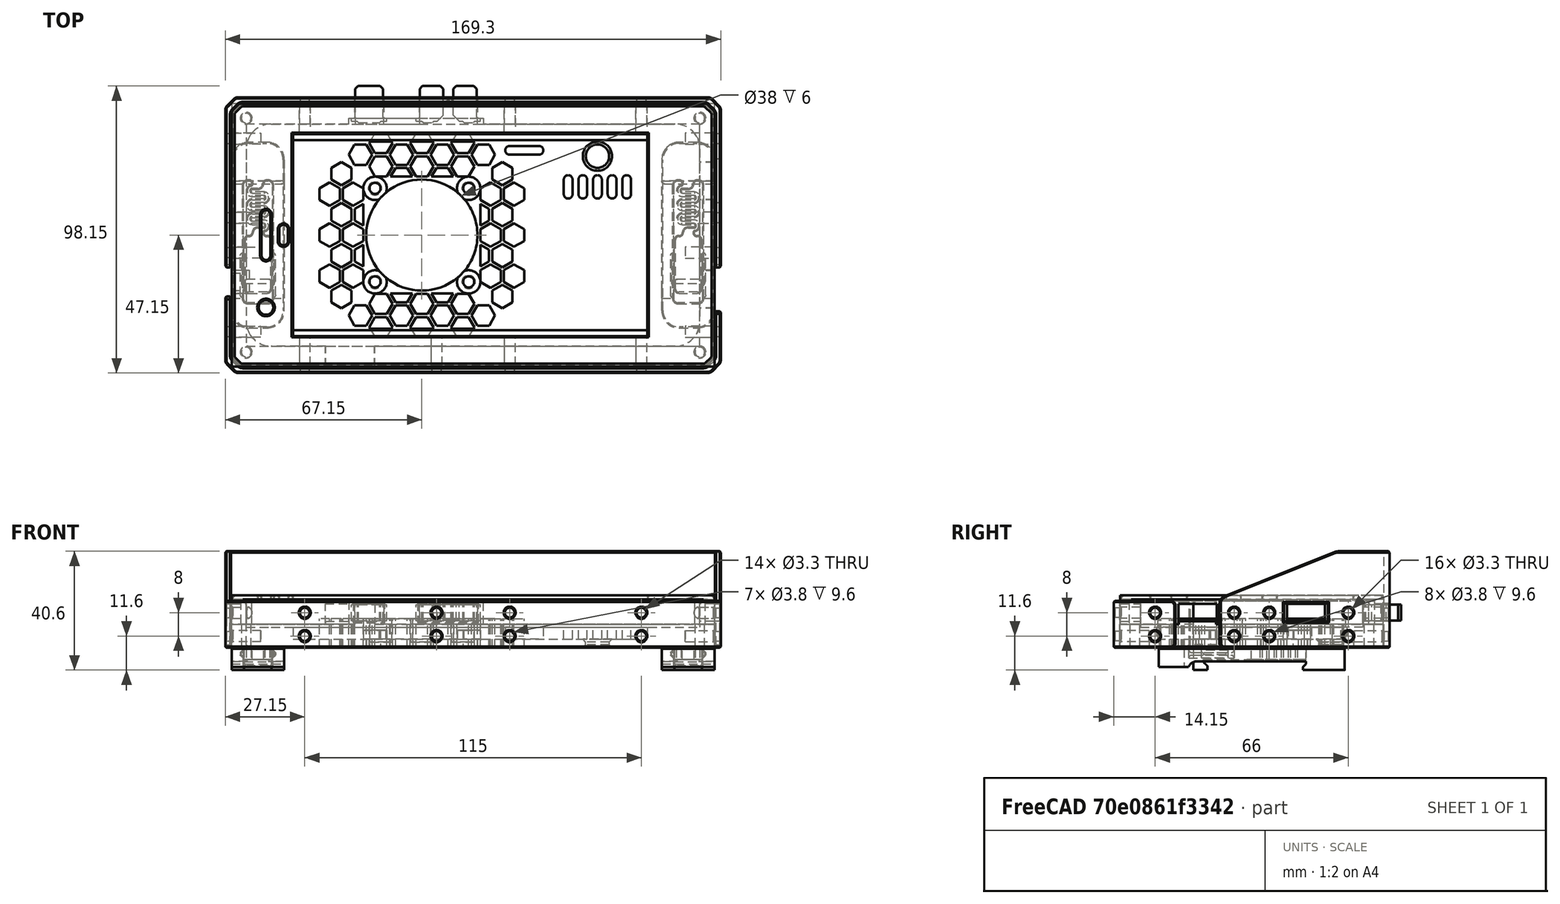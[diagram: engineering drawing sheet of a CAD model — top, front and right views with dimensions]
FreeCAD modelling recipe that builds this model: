
FCSTD DOCUMENT  (FreeCAD 0.19R24291 (Git))
Label: pixel-xl-navi-case
License: Other
LicenseURL: GPL3
objects: Sketcher::SketchObject×37, PartDesign::Pocket×27, PartDesign::Chamfer×20, Part::Box×14, PartDesign::Plane×12, PartDesign::Pad×10, PartDesign::Fillet×9, Part::Feature×8, Part::Chamfer×5, Part::MultiFuse×4, PartDesign::Body×4, Part::Cut×2, Spreadsheet::Sheet×1, Mesh::Feature×1, Part::FeaturePython×1
note: 219 computed .brp shape members not serialized (recipe doc carries the construction recipe); baked Part::Feature solids carry a one-line shape summary decoded from their .brp

FEATURE [Spreadsheet::Sheet] Spreadsheet  label="args"
  cells = A2=pixel width; B2(pixel_w)=155; A3=pixel heigh; B3(pixel_h)=76; A4=pixel thickness; B4(pixel_t)=8; A5=top screen offset; B5(screen_top_offset)=16; A6=bottom screen offset; B6(screen_bottom_offset)=17; A7=side screen offset; B7(screen_side_offset)=3.5; A8=power button offset; B8(button_power_offset)=37; A9=volume button offset; B9(button_volume_offset)=59; A10=power button width; B10(button_power_width)=10; A11=volume button width; B11(button_volume_width)=20; A12=screen width; B12(screen_width)=121; A13=screen heigh; B13(screen_heigh)=69; A14=pixel corner radius; B14(pixel_corner_radius)=8.5; A18=case thickness; B18(case_thickness)=10; A19=case width offset; B19(case_width_offset)=5; A20=case heigh offset; B20(case_heigh_offset)=7; A21=case corner radius; B21(case_corner_radius)=3; A23=front speaker offset; B23(front_speaker_offset)=5.75; A24=front speaker width; B24(front_speaker_width)=2; A25=front speaker heigh; B25(front_speaker_heigh)=16; A27=light sensor width; B27(light_sensor_width)=2; A28=light sensor heigh; B28(light_sensor_heigh)=6; A29=light sensor offset; B29(light_sensor_offset)=11.75; A31=camera x offset; B31(camera_x_offset)=6.75; A32=camera y offset; B32(camera_y_offset)=13.25; A33=camera radius; B33(camera_radius)=2; A35=speaker offset; B35(spekaer_offset)=14; A36=speaker width; B36(speaker_width)=11; A39=back thickness; B39(back_thickness)=8; A41=fan offset; B41(fan_offset)=60; A43=wiring hole offset; B43(wiring_hole_offset)=120; A44=wiring hole radius; B44(wiring_hole_radius)=4; A46=sim slot offset; B46(sim_slot_offset)=28; A47=sim slot width; B47(sim_slot_width)=15; A49=headphone jack center offset; B49(headphone_jack_center_offset)=22; A50=headphone jack radius; B50(headphone_jack_radius)=5; A51=headphone_jack_width; B51(headphone_jack_width)=8; A53=sun visor heigh; B53(sun_visor_heigh)=15; A54=sun visor ramp width; B54(sun_visor_ramp_width)=40
FEATURE [Sketcher::SketchObject] Sketch
  FullyConstrained = true
  MapMode = 5
  Support = -> [XY_Plane]
  expr: Constraints[11] = <<args>>.pixel_w + <<args>>.case_width_offset
  expr: Constraints[10] = <<args>>.pixel_h + <<args>>.case_heigh_offset
  expr: Constraints[9] = <<args>>.case_width_offset
  expr: Constraints[8] = <<args>>.case_heigh_offset
  sketch-geometry (4):
    g0: LineSegment StartX=-5 StartY=-7 StartZ=0 EndX=160 EndY=-7 EndZ=0
    g1: LineSegment StartX=160 StartY=-7 StartZ=0 EndX=160 EndY=83 EndZ=0
    g2: LineSegment StartX=160 StartY=83 StartZ=0 EndX=-5 EndY=83 EndZ=0
    g3: LineSegment StartX=-5 StartY=83 StartZ=0 EndX=-5 EndY=-7 EndZ=0
  constraints (12):
    c: Coincident(g0,g1)
    c: Coincident(g1,g2)
    c: Coincident(g2,g3)
    c: Coincident(g3,g0)
    c: Horizontal(g0)
    c: Horizontal(g2)
    c: Vertical(g1)
    c: Vertical(g3)
    c: DistanceY(g0,g-1) = 7
    c: DistanceX(g0,g-1) = 5
    c: DistanceY(g-1,g2) = 83
    c: DistanceX(g-1,g1) = 160
FEATURE [PartDesign::Pad] Pad
  Direction = (1,1,1)
  Length = 10
  Length2 = 100
  Profile = -> Sketch
  Type = 0
  expr: Length = <<args>>.case_thickness
FEATURE [PartDesign::Plane] DatumPlane  label="face-plane"
  AttachmentOffset = pos=(0,0,10) rot=(0,0,1;0rad)
  Length = 213.27
  MapMode = 5
  Placement = pos=(0,0,10) rot=(0,0,1;0rad)
  ResizeMode = 0
  Support = -> [XY_Plane]
  Width = 136.27
  expr: .AttachmentOffset.Base.z = <<args>>.case_thickness
FEATURE [Sketcher::SketchObject] Sketch001
  FullyConstrained = true
  MapMode = 5
  Placement = pos=(0,0,10) rot=(0,0,1;0rad)
  Support = -> [DatumPlane]
  expr: Constraints[11] = <<args>>.screen_heigh
  expr: Constraints[10] = <<args>>.screen_width
  expr: Constraints[9] = <<args>>.screen_side_offset
  expr: Constraints[8] = <<args>>.screen_top_offset
  sketch-geometry (4):
    g0: LineSegment StartX=16 StartY=72.5 StartZ=0 EndX=137 EndY=72.5 EndZ=0
    g1: LineSegment StartX=137 StartY=72.5 StartZ=0 EndX=137 EndY=3.5 EndZ=0
    g2: LineSegment StartX=137 StartY=3.5 StartZ=0 EndX=16 EndY=3.5 EndZ=0
    g3: LineSegment StartX=16 StartY=3.5 StartZ=0 EndX=16 EndY=72.5 EndZ=0
  constraints (12):
    c: Coincident(g0,g1)
    c: Coincident(g1,g2)
    c: Coincident(g2,g3)
    c: Coincident(g3,g0)
    c: Horizontal(g0)
    c: Horizontal(g2)
    c: Vertical(g1)
    c: Vertical(g3)
    c: DistanceX(g-1,g2) = 16
    c: DistanceY(g-1,g2) = 3.5
    c: DistanceX(g0,g0) = 121
    c: DistanceY(g1,g1) = 69
FEATURE [PartDesign::Pocket] Pocket
  BaseFeature = -> Pad
  Length = 5
  Length2 = 100
  Profile = -> Sketch001
  Type = 1
FEATURE [PartDesign::Plane] DatumPlane001  label="zero-plane"
  Length = 213.27
  MapMode = 5
  ResizeMode = 0
  Support = -> [XY_Plane]
  Width = 136.27
FEATURE [Sketcher::SketchObject] Sketch002
  FullyConstrained = true
  MapMode = 5
  Support = -> [DatumPlane001]
  expr: Constraints[10] = <<args>>.pixel_h
  expr: Constraints[9] = <<args>>.pixel_w
  sketch-geometry (4):
    g0: LineSegment StartX=0 StartY=0 StartZ=0 EndX=155 EndY=0 EndZ=0
    g1: LineSegment StartX=155 StartY=0 StartZ=0 EndX=155 EndY=76 EndZ=0
    g2: LineSegment StartX=155 StartY=76 StartZ=0 EndX=0 EndY=76 EndZ=0
    g3: LineSegment StartX=0 StartY=76 StartZ=0 EndX=0 EndY=0 EndZ=0
  constraints (11):
    c: Coincident(g0,g1)
    c: Coincident(g1,g2)
    c: Coincident(g2,g3)
    c: Coincident(g3,g0)
    c: Horizontal(g0)
    c: Horizontal(g2)
    c: Vertical(g1)
    c: Vertical(g3)
    c: Coincident(g0,g-1)
    c: DistanceX(g2,g2) = 155
    c: DistanceY(g1,g1) = 76
FEATURE [PartDesign::Pocket] Pocket001
  BaseFeature = -> Pocket
  Length = 8
  Length2 = 100
  Profile = -> Sketch002
  Reversed = true
  Type = 0
  expr: Length = <<args>>.case_thickness - 2
FEATURE [Sketcher::SketchObject] Sketch003
  FullyConstrained = true
  MapMode = 5
  Placement = pos=(0,0,10) rot=(0,0,1;0rad)
  Support = -> [DatumPlane]
  expr: Constraints[21] = <<args>>.light_sensor_heigh - <<args>>.light_sensor_width
  expr: Constraints[19] = <<args>>.light_sensor_width / 2 + 0.5
  expr: Constraints[18] = <<args>>.front_speaker_width / 2 + 0.5
  expr: Constraints[16] = (<<args>>.pixel_h - <<args>>.front_speaker_heigh) / 2 + <<args>>.front_speaker_width / 2
  expr: Constraints[20] = <<args>>.light_sensor_offset + <<args>>.light_sensor_width / 2
  expr: Constraints[15] = <<args>>.front_speaker_offset + <<args>>.front_speaker_width / 2
  expr: Constraints[22] = (<<args>>.pixel_h - <<args>>.light_sensor_heigh) / 2 + <<args>>.light_sensor_width / 2
  expr: Constraints[17] = <<args>>.front_speaker_heigh - <<args>>.front_speaker_width
  expr: Constraints[14] = <<args>>.camera_y_offset
  expr: Constraints[13] = <<args>>.camera_x_offset
  expr: Constraints[12] = <<args>>.camera_radius + 0.5
  sketch-geometry (9):
    g0: ArcOfCircle CenterX=6.75 CenterY=45 CenterZ=0 NormalX=0 NormalY=0 NormalZ=1 AngleXU=0 Radius=1.5 StartAngle=2e-16 EndAngle=3.14159
    g1: ArcOfCircle CenterX=6.75 CenterY=31 CenterZ=0 NormalX=0 NormalY=0 NormalZ=1 AngleXU=0 Radius=1.5 StartAngle=3.14159 EndAngle=6.28319
    g2: LineSegment StartX=5.25 StartY=45 StartZ=0 EndX=5.25 EndY=31 EndZ=0
    g3: LineSegment StartX=8.25 StartY=45 StartZ=0 EndX=8.25 EndY=31 EndZ=0
    g4: ArcOfCircle CenterX=12.75 CenterY=40 CenterZ=0 NormalX=0 NormalY=0 NormalZ=1 AngleXU=0 Radius=1.5 StartAngle=2.4e-15 EndAngle=3.14159
    g5: ArcOfCircle CenterX=12.75 CenterY=36 CenterZ=0 NormalX=0 NormalY=0 NormalZ=1 AngleXU=0 Radius=1.5 StartAngle=3.14159 EndAngle=6.28319
    g6: LineSegment StartX=11.25 StartY=40 StartZ=0 EndX=11.25 EndY=36 EndZ=0
    g7: LineSegment StartX=14.25 StartY=40 StartZ=0 EndX=14.25 EndY=36 EndZ=0
    g8: Circle CenterX=6.75 CenterY=13.25 CenterZ=0 NormalX=0 NormalY=0 NormalZ=1 AngleXU=0 Radius=2.5
  constraints (23):
    c: Tangent(g0,g3) = 1.5708
    c: Tangent(g0,g2) = -1.5708
    c: Tangent(g2,g1) = -1.5708
    c: Tangent(g3,g1) = 1.5708
    c: Vertical(g2)
    c: Equal(g0,g1)
    c: Tangent(g4,g7) = 1.5708
    c: Tangent(g4,g6) = -1.5708
    c: Tangent(g6,g5) = -1.5708
    c: Tangent(g7,g5) = 1.5708
    c: Vertical(g6)
    c: Equal(g4,g5)
    c: Radius(g8) = 2.5
    c: DistanceX(g-1,g8) = 6.75
    c: DistanceY(g-1,g8) = 13.25
    c: DistanceX(g-1,g1) = 6.75
    c: DistanceY(g-1,g1) = 31
    c: DistanceY(g1,g0) = 14
    c: Radius(g0) = 1.5
    c: Radius(g4) = 1.5
    c: DistanceX(g-1,g5) = 12.75
    c: DistanceY(g5,g4) = 4
    c: DistanceY(g-1,g5) = 36
FEATURE [PartDesign::Pocket] Pocket002
  BaseFeature = -> Pocket001
  Length = 5
  Length2 = 100
  Profile = -> Sketch003
  Type = 1
FEATURE [PartDesign::Plane] DatumPlane002  label="right-edge-plane"
  AttachmentOffset = pos=(0,0,-83) rot=(0,0,1;0rad)
  Length = 204.235
  MapMode = 5
  Placement = pos=(0,83,1.84e-14) rot=(1,0,0;1.5708rad)
  ResizeMode = 0
  Support = -> [XZ_Plane]
  Width = 69.2354
  expr: .AttachmentOffset.Base.z = -(<<args>>.pixel_h + <<args>>.case_heigh_offset)
FEATURE [Sketcher::SketchObject] Sketch007
  FullyConstrained = true
  MapMode = 5
  Placement = pos=(0,83,1.84e-14) rot=(1,0,0;1.5708rad)
  Support = -> [DatumPlane002]
  expr: Constraints[16] = <<args>>.button_power_width
  expr: Constraints[17] = <<args>>.button_volume_width
  expr: Constraints[18] = <<args>>.button_volume_offset
  expr: Constraints[19] = <<args>>.button_power_offset
  sketch-geometry (8):
    g0: LineSegment StartX=37 StartY=7 StartZ=0 EndX=47 EndY=7 EndZ=0
    g1: LineSegment StartX=47 StartY=7 StartZ=0 EndX=47 EndY=0 EndZ=0
    g2: LineSegment StartX=47 StartY=0 StartZ=0 EndX=37 EndY=0 EndZ=0
    g3: LineSegment StartX=37 StartY=0 StartZ=0 EndX=37 EndY=7 EndZ=0
    g4: LineSegment StartX=59 StartY=7 StartZ=0 EndX=79 EndY=7 EndZ=0
    g5: LineSegment StartX=79 StartY=7 StartZ=0 EndX=79 EndY=0 EndZ=0
    g6: LineSegment StartX=79 StartY=0 StartZ=0 EndX=59 EndY=0 EndZ=0
    g7: LineSegment StartX=59 StartY=0 StartZ=0 EndX=59 EndY=7 EndZ=0
  constraints (24):
    c: Coincident(g0,g1)
    c: Coincident(g1,g2)
    c: Coincident(g2,g3)
    c: Coincident(g3,g0)
    c: Horizontal(g0)
    c: Horizontal(g2)
    c: Vertical(g1)
    c: Vertical(g3)
    c: Coincident(g4,g5)
    c: Coincident(g5,g6)
    c: Coincident(g6,g7)
    c: Coincident(g7,g4)
    c: Horizontal(g4)
    c: Horizontal(g6)
    c: Vertical(g5)
    c: Vertical(g7)
    c: DistanceX(g2,g2) = 10
    c: DistanceX(g6,g6) = 20
    c: DistanceX(g-1,g6) = 59
    c: DistanceX(g-1,g2) = 37
    c: DistanceY(g-1,g2) = 0
    c: DistanceY(g-1,g6) = 0
    c: DistanceY(g3,g3) = 7
    c: DistanceY(g7,g7) = 7
FEATURE [PartDesign::Plane] DatumPlane003  label="bottom-edge-plane"
  AttachmentOffset = pos=(0,0,160) rot=(0,0,1;0rad)
  Length = 122.697
  MapMode = 5
  Placement = pos=(160,-3.55e-14,3.55e-14) rot=(0.57735,0.57735,0.57735;2.0944rad)
  ResizeMode = 0
  Support = -> [YZ_Plane]
  Width = 64.6969
  expr: .AttachmentOffset.Base.z = <<args>>.pixel_w + <<args>>.case_width_offset
FEATURE [Sketcher::SketchObject] Sketch008
  FullyConstrained = true
  MapMode = 5
  Placement = pos=(160,-3.55e-14,3.55e-14) rot=(0.57735,0.57735,0.57735;2.0944rad)
  Support = -> [DatumPlane003]
  expr: Constraints[18] = <<args>>.speaker_width + 2
  expr: Constraints[19] = <<args>>.speaker_width + 2
  expr: Constraints[23] = <<args>>.pixel_h - (<<args>>.spekaer_offset + <<args>>.speaker_width + 2 - 1)
  expr: Constraints[20] = <<args>>.spekaer_offset - 1
  sketch-geometry (8):
    g0: LineSegment StartX=13 StartY=0 StartZ=0 EndX=26 EndY=0 EndZ=0
    g1: LineSegment StartX=26 StartY=0 StartZ=0 EndX=26 EndY=7 EndZ=0
    g2: LineSegment StartX=26 StartY=7 StartZ=0 EndX=13 EndY=7 EndZ=0
    g3: LineSegment StartX=13 StartY=7 StartZ=0 EndX=13 EndY=0 EndZ=0
    g4: LineSegment StartX=50 StartY=0 StartZ=0 EndX=63 EndY=0 EndZ=0
    g5: LineSegment StartX=63 StartY=0 StartZ=0 EndX=63 EndY=7 EndZ=0
    g6: LineSegment StartX=63 StartY=7 StartZ=0 EndX=50 EndY=7 EndZ=0
    g7: LineSegment StartX=50 StartY=7 StartZ=0 EndX=50 EndY=0 EndZ=0
  constraints (24):
    c: Coincident(g0,g1)
    c: Coincident(g1,g2)
    c: Coincident(g2,g3)
    c: Coincident(g3,g0)
    c: Horizontal(g0)
    c: Horizontal(g2)
    c: Vertical(g1)
    c: Vertical(g3)
    c: Coincident(g4,g5)
    c: Coincident(g5,g6)
    c: Coincident(g6,g7)
    c: Coincident(g7,g4)
    c: Horizontal(g4)
    c: Horizontal(g6)
    c: Vertical(g5)
    c: Vertical(g7)
    c: DistanceY(g-1,g0) = 0
    c: DistanceY(g-1,g4) = 0
    c: DistanceX(g2,g2) = 13
    c: DistanceX(g6,g6) = 13
    c: DistanceX(g-1,g0) = 13
    c: DistanceY(g1,g1) = 7
    c: DistanceY(g7,g7) = 7
    c: DistanceX(g-1,g4) = 50
FEATURE [Mesh::Feature] PixelXL
  Placement = pos=(77,38,8) rot=(0.707107,-0.707107,0;3.14159rad)
FEATURE [PartDesign::Plane] DatumPlane004  label="left-edge-plane"
  AttachmentOffset = pos=(0,0,7) rot=(0,0,1;0rad)
  Length = 204.235
  MapMode = 5
  Placement = pos=(0,-7,-1.6e-15) rot=(1,0,0;1.5708rad)
  ResizeMode = 0
  Support = -> [XZ_Plane]
  Width = 69.2354
  expr: .AttachmentOffset.Base.z = <<args>>.case_heigh_offset
FEATURE [Sketcher::SketchObject] Sketch009
  FullyConstrained = true
  MapMode = 5
  Placement = pos=(0,-7,-1.6e-15) rot=(1,0,0;1.5708rad)
  Support = -> [DatumPlane004]
  expr: Constraints[8] = <<args>>.sim_slot_offset - 1
  expr: Constraints[9] = <<args>>.sim_slot_width + 2
  expr: Constraints[10] = <<args>>.pixel_t - 1
  sketch-geometry (4):
    g0: LineSegment StartX=27 StartY=7 StartZ=0 EndX=44 EndY=7 EndZ=0
    g1: LineSegment StartX=44 StartY=7 StartZ=0 EndX=44 EndY=0 EndZ=0
    g2: LineSegment StartX=44 StartY=0 StartZ=0 EndX=27 EndY=0 EndZ=0
    g3: LineSegment StartX=27 StartY=0 StartZ=0 EndX=27 EndY=7 EndZ=0
  constraints (12):
    c: Coincident(g0,g1)
    c: Coincident(g1,g2)
    c: Coincident(g2,g3)
    c: Coincident(g3,g0)
    c: Horizontal(g0)
    c: Horizontal(g2)
    c: Vertical(g1)
    c: Vertical(g3)
    c: DistanceX(g-1,g2) = 27
    c: DistanceX(g0,g0) = 17
    c: DistanceY(g1,g1) = 7
    c: DistanceY(g-1,g2) = 0
FEATURE [PartDesign::Plane] DatumPlane005  label="top-edge-plane"
  AttachmentOffset = pos=(0,0,-7) rot=(0,0,1;0rad)
  Length = 122.697
  MapMode = 5
  Placement = pos=(-7,1.6e-15,-1.6e-15) rot=(0.57735,0.57735,0.57735;2.0944rad)
  ResizeMode = 0
  Support = -> [YZ_Plane]
  Width = 64.6969
  expr: .AttachmentOffset.Base.z = -<<args>>.case_heigh_offset
FEATURE [Sketcher::SketchObject] Sketch010
  FullyConstrained = true
  MapMode = 5
  Placement = pos=(-7,1.6e-15,-1.6e-15) rot=(0.57735,0.57735,0.57735;2.0944rad)
  Support = -> [DatumPlane005]
  expr: Constraints[8] = <<args>>.headphone_jack_center_offset - <<args>>.headphone_jack_width / 2
  expr: Constraints[9] = <<args>>.headphone_jack_width
  expr: Constraints[10] = <<args>>.pixel_t
  sketch-geometry (4):
    g0: LineSegment StartX=18 StartY=8 StartZ=0 EndX=26 EndY=8 EndZ=0
    g1: LineSegment StartX=26 StartY=8 StartZ=0 EndX=26 EndY=0 EndZ=0
    g2: LineSegment StartX=26 StartY=0 StartZ=0 EndX=18 EndY=0 EndZ=0
    g3: LineSegment StartX=18 StartY=0 StartZ=0 EndX=18 EndY=8 EndZ=0
  constraints (12):
    c: Coincident(g0,g1)
    c: Coincident(g1,g2)
    c: Coincident(g2,g3)
    c: Coincident(g3,g0)
    c: Horizontal(g0)
    c: Horizontal(g2)
    c: Vertical(g1)
    c: Vertical(g3)
    c: DistanceX(g-1,g2) = 18
    c: DistanceX(g2,g2) = 8
    c: DistanceY(g3,g3) = 8
    c: DistanceY(g-1,g2) = 0
FEATURE [PartDesign::Plane] DatumPlane006  label="zero-plane001"
  Length = 213.27
  MapMode = 5
  ResizeMode = 0
  Support = -> [XY_Plane001]
  Width = 136.27
FEATURE [Sketcher::SketchObject] Sketch011
  FullyConstrained = true
  MapMode = 5
  Support = -> [DatumPlane006]
  expr: Constraints[11] = <<args>>.case_heigh_offset
  expr: Constraints[10] = <<args>>.case_width_offset
  expr: Constraints[9] = <<args>>.case_heigh_offset * 2 + <<args>>.pixel_h
  expr: Constraints[8] = <<args>>.case_width_offset * 2 + <<args>>.pixel_w
  sketch-geometry (4):
    g0: LineSegment StartX=-5 StartY=-7 StartZ=0 EndX=160 EndY=-7 EndZ=0
    g1: LineSegment StartX=160 StartY=-7 StartZ=0 EndX=160 EndY=83 EndZ=0
    g2: LineSegment StartX=160 StartY=83 StartZ=0 EndX=-5 EndY=83 EndZ=0
    g3: LineSegment StartX=-5 StartY=83 StartZ=0 EndX=-5 EndY=-7 EndZ=0
  constraints (12):
    c: Coincident(g0,g1)
    c: Coincident(g1,g2)
    c: Coincident(g2,g3)
    c: Coincident(g3,g0)
    c: Horizontal(g0)
    c: Horizontal(g2)
    c: Vertical(g1)
    c: Vertical(g3)
    c: DistanceX(g2,g2) = 165
    c: DistanceY(g1,g1) = 90
    c: DistanceX(g0,g-1) = 5
    c: DistanceY(g0,g-1) = 7
FEATURE [PartDesign::Pad] Pad001
  Direction = (1,1,1)
  Length = 8
  Length2 = 100
  Profile = -> Sketch011
  Type = 0
  expr: Length = <<args>>.back_thickness
FEATURE [PartDesign::Plane] DatumPlane007  label="inner-face-plane"
  AttachmentOffset = pos=(0,0,8) rot=(0,0,1;0rad)
  Length = 213.27
  MapMode = 5
  Placement = pos=(0,0,8) rot=(0,0,1;0rad)
  ResizeMode = 0
  Support = -> [XY_Plane001]
  Width = 136.27
  expr: .AttachmentOffset.Base.z = <<args>>.back_thickness
FEATURE [Sketcher::SketchObject] Sketch012
  FullyConstrained = true
  MapMode = 5
  Placement = pos=(0,0,8) rot=(0,0,1;0rad)
  Support = -> [DatumPlane007]
  expr: Constraints[11] = <<args>>.screen_top_offset
  expr: Constraints[10] = <<args>>.screen_side_offset + 2
  expr: Constraints[9] = <<args>>.screen_width
  expr: Constraints[8] = <<args>>.screen_heigh - 4
  sketch-geometry (4):
    g0: LineSegment StartX=16 StartY=5.5 StartZ=0 EndX=137 EndY=5.5 EndZ=0
    g1: LineSegment StartX=137 StartY=5.5 StartZ=0 EndX=137 EndY=70.5 EndZ=0
    g2: LineSegment StartX=137 StartY=70.5 StartZ=0 EndX=16 EndY=70.5 EndZ=0
    g3: LineSegment StartX=16 StartY=70.5 StartZ=0 EndX=16 EndY=5.5 EndZ=0
  constraints (12):
    c: Coincident(g0,g1)
    c: Coincident(g1,g2)
    c: Coincident(g2,g3)
    c: Coincident(g3,g0)
    c: Horizontal(g0)
    c: Horizontal(g2)
    c: Vertical(g1)
    c: Vertical(g3)
    c: DistanceY(g1,g1) = 65
    c: DistanceX(g2,g2) = 121
    c: DistanceY(g-1,g0) = 5.5
    c: DistanceX(g-1,g0) = 16
FEATURE [PartDesign::Pocket] Pocket009
  BaseFeature = -> Pad001
  Length = 5
  Length2 = 100
  Profile = -> Sketch012
  Type = 0
FEATURE [PartDesign::Plane] DatumPlane009  label="left-edge-plane001"
  AttachmentOffset = pos=(0,0,7) rot=(0,0,1;0rad)
  Length = 204.235
  MapMode = 5
  Placement = pos=(0,-7,-1.6e-15) rot=(1,0,0;1.5708rad)
  ResizeMode = 0
  Support = -> [XZ_Plane001]
  Width = 69.2354
  expr: .AttachmentOffset.Base.z = <<args>>.case_heigh_offset
FEATURE [PartDesign::Plane] DatumPlane010  label="top-edge-plane001"
  AttachmentOffset = pos=(0,0,-5) rot=(0,0,1;0rad)
  Length = 122.697
  MapMode = 5
  Placement = pos=(-5,1.1e-15,-1.1e-15) rot=(0.57735,0.57735,0.57735;2.0944rad)
  ResizeMode = 0
  Support = -> [YZ_Plane001]
  Width = 64.6969
  expr: .AttachmentOffset.Base.z = -<<args>>.case_width_offset
FEATURE [PartDesign::Plane] DatumPlane011  label="bottom-edge-plane001"
  AttachmentOffset = pos=(0,0,160) rot=(0,0,1;0rad)
  Length = 122.697
  MapMode = 5
  Placement = pos=(160,-3.55e-14,3.55e-14) rot=(0.57735,0.57735,0.57735;2.0944rad)
  ResizeMode = 0
  Support = -> [YZ_Plane001]
  Width = 64.6969
  expr: .AttachmentOffset.Base.z = <<args>>.pixel_w + <<args>>.case_width_offset
FEATURE [PartDesign::Plane] DatumPlane012  label="right-edge-plane001"
  AttachmentOffset = pos=(0,0,-83) rot=(0,0,1;0rad)
  Length = 204.235
  MapMode = 5
  Placement = pos=(0,83,1.84e-14) rot=(1,0,0;1.5708rad)
  ResizeMode = 0
  Support = -> [XZ_Plane001]
  Width = 69.2354
  expr: .AttachmentOffset.Base.z = -(<<args>>.pixel_h + <<args>>.case_heigh_offset)
FEATURE [Sketcher::SketchObject] Sketch013
  FullyConstrained = true
  MapMode = 5
  Placement = pos=(0,83,1.84e-14) rot=(1,0,0;1.5708rad)
  Support = -> [DatumPlane012]
  expr: Constraints[23] = <<args>>.button_volume_offset + 0.15
  expr: Constraints[21] = <<args>>.button_volume_width - 0.3
  expr: Constraints[20] = <<args>>.button_power_width - 0.3
  expr: Constraints[22] = <<args>>.button_power_offset + 0.15
  expr: Constraints[17] = <<args>>.back_thickness
  expr: Constraints[16] = <<args>>.back_thickness
  sketch-geometry (8):
    g0: LineSegment StartX=37.15 StartY=9 StartZ=0 EndX=46.85 EndY=9 EndZ=0
    g1: LineSegment StartX=46.85 StartY=9 StartZ=0 EndX=46.85 EndY=8 EndZ=0
    g2: LineSegment StartX=46.85 StartY=8 StartZ=0 EndX=37.15 EndY=8 EndZ=0
    g3: LineSegment StartX=37.15 StartY=8 StartZ=0 EndX=37.15 EndY=9 EndZ=0
    g4: LineSegment StartX=59.15 StartY=9 StartZ=0 EndX=78.85 EndY=9 EndZ=0
    g5: LineSegment StartX=78.85 StartY=9 StartZ=0 EndX=78.85 EndY=8 EndZ=0
    g6: LineSegment StartX=78.85 StartY=8 StartZ=0 EndX=59.15 EndY=8 EndZ=0
    g7: LineSegment StartX=59.15 StartY=8 StartZ=0 EndX=59.15 EndY=9 EndZ=0
  constraints (24):
    c: Coincident(g0,g1)
    c: Coincident(g1,g2)
    c: Coincident(g2,g3)
    c: Coincident(g3,g0)
    c: Horizontal(g0)
    c: Horizontal(g2)
    c: Vertical(g1)
    c: Vertical(g3)
    c: Coincident(g4,g5)
    c: Coincident(g5,g6)
    c: Coincident(g6,g7)
    c: Coincident(g7,g4)
    c: Horizontal(g4)
    c: Horizontal(g6)
    c: Vertical(g5)
    c: Vertical(g7)
    c: DistanceY(g-1,g2) = 8
    c: DistanceY(g-1,g6) = 8
    c: DistanceY(g3,g3) = 1
    c: DistanceY(g7,g7) = 1
    c: DistanceX(g0,g0) = 9.7
    c: DistanceX(g4,g4) = 19.7
    c: DistanceX(g-1,g2) = 37.15
    c: DistanceX(g-1,g6) = 59.15
FEATURE [PartDesign::Pad] Pad002  label="right-pad"
  BaseFeature = -> Pocket009
  Direction = (1,1,1)
  Length = 7
  Length2 = 100
  Profile = -> Sketch013
  Type = 0
  expr: Length = <<args>>.case_heigh_offset
FEATURE [Sketcher::SketchObject] Sketch014
  FullyConstrained = true
  MapMode = 5
  Placement = pos=(160,-3.55e-14,3.55e-14) rot=(0.57735,0.57735,0.57735;2.0944rad)
  Support = -> [DatumPlane011]
  expr: Constraints[23] = <<args>>.pixel_h - (<<args>>.spekaer_offset + <<args>>.speaker_width + 2 - 1) + 0.15
  expr: Constraints[19] = <<args>>.back_thickness
  expr: Constraints[18] = <<args>>.back_thickness
  expr: Constraints[22] = <<args>>.spekaer_offset + 0.15 - 1
  expr: Constraints[17] = <<args>>.speaker_width - 0.3 + 2
  expr: Constraints[16] = <<args>>.speaker_width - 0.3 + 2
  sketch-geometry (8):
    g0: LineSegment StartX=13.15 StartY=9 StartZ=0 EndX=25.85 EndY=9 EndZ=0
    g1: LineSegment StartX=25.85 StartY=9 StartZ=0 EndX=25.85 EndY=8 EndZ=0
    g2: LineSegment StartX=25.85 StartY=8 StartZ=0 EndX=13.15 EndY=8 EndZ=0
    g3: LineSegment StartX=13.15 StartY=8 StartZ=0 EndX=13.15 EndY=9 EndZ=0
    g4: LineSegment StartX=50.15 StartY=9 StartZ=0 EndX=62.85 EndY=9 EndZ=0
    g5: LineSegment StartX=62.85 StartY=9 StartZ=0 EndX=62.85 EndY=8 EndZ=0
    g6: LineSegment StartX=62.85 StartY=8 StartZ=0 EndX=50.15 EndY=8 EndZ=0
    g7: LineSegment StartX=50.15 StartY=8 StartZ=0 EndX=50.15 EndY=9 EndZ=0
  constraints (24):
    c: Coincident(g0,g1)
    c: Coincident(g1,g2)
    c: Coincident(g2,g3)
    c: Coincident(g3,g0)
    c: Horizontal(g0)
    c: Horizontal(g2)
    c: Vertical(g1)
    c: Vertical(g3)
    c: Coincident(g4,g5)
    c: Coincident(g5,g6)
    c: Coincident(g6,g7)
    c: Coincident(g7,g4)
    c: Horizontal(g4)
    c: Horizontal(g6)
    c: Vertical(g5)
    c: Vertical(g7)
    c: DistanceX(g0,g0) = 12.7
    c: DistanceX(g4,g4) = 12.7
    c: DistanceY(g-1,g2) = 8
    c: DistanceY(g-1,g6) = 8
    c: DistanceY(g3,g3) = 1
    c: DistanceY(g7,g7) = 1
    c: DistanceX(g-1,g2) = 13.15
    c: DistanceX(g-1,g6) = 50.15
FEATURE [PartDesign::Pad] Pad003  label="bottom-pad"
  BaseFeature = -> Pad002
  Direction = (1,1,1)
  Length = 5
  Length2 = 100
  Profile = -> Sketch014
  Reversed = true
  Type = 0
  expr: Length = <<args>>.case_width_offset
FEATURE [Sketcher::SketchObject] Sketch015
  FullyConstrained = true
  MapMode = 5
  Support = -> [DatumPlane001]
  expr: Constraints[11] = <<args>>.pixel_w
  expr: Constraints[10] = <<args>>.pixel_w
  expr: Constraints[8] = <<args>>.pixel_h + 2
  expr: Constraints[7] = <<args>>.pixel_h + 2
  sketch-geometry (4):
    g0: Circle CenterX=0 CenterY=-2 CenterZ=0 NormalX=0 NormalY=0 NormalZ=1 AngleXU=0 Radius=1.9
    g1: Circle CenterX=0 CenterY=78 CenterZ=0 NormalX=0 NormalY=0 NormalZ=1 AngleXU=0 Radius=1.9
    g2: Circle CenterX=155 CenterY=78 CenterZ=0 NormalX=0 NormalY=0 NormalZ=1 AngleXU=0 Radius=1.9
    g3: Circle CenterX=155 CenterY=-2 CenterZ=0 NormalX=0 NormalY=0 NormalZ=1 AngleXU=0 Radius=1.9
  constraints (12):
    c: Radius(g2) = 1.9
    c: Radius(g3) = 1.9
    c: Radius(g1) = 1.9
    c: Radius(g0) = 1.9
    c: DistanceY(g0,g-1) = 2
    c: DistanceX(g0,g-1) = 0
    c: DistanceX(g1,g-1) = 0
    c: DistanceY(g-1,g1) = 78
    c: DistanceY(g-1,g2) = 78
    c: DistanceY(g3,g0) = 0
    c: DistanceX(g-1,g2) = 155
    c: DistanceX(g-1,g3) = 155
FEATURE [Sketcher::SketchObject] Sketch016
  FullyConstrained = true
  MapMode = 5
  Support = -> [DatumPlane006]
  expr: Constraints[11] = <<args>>.pixel_w
  expr: Constraints[10] = <<args>>.pixel_w
  expr: Constraints[7] = <<args>>.pixel_h + 2
  expr: Constraints[6] = <<args>>.pixel_h + 2
  sketch-geometry (4):
    g0: Circle CenterX=0 CenterY=78 CenterZ=0 NormalX=0 NormalY=0 NormalZ=1 AngleXU=0 Radius=1.65
    g1: Circle CenterX=155 CenterY=78 CenterZ=0 NormalX=0 NormalY=0 NormalZ=1 AngleXU=0 Radius=1.65
    g2: Circle CenterX=155 CenterY=-2 CenterZ=0 NormalX=0 NormalY=0 NormalZ=1 AngleXU=0 Radius=1.65
    g3: Circle CenterX=0 CenterY=-2 CenterZ=0 NormalX=0 NormalY=0 NormalZ=1 AngleXU=0 Radius=1.65
  constraints (12):
    c: Radius(g3) = 1.65
    c: Radius(g0) = 1.65
    c: Radius(g1) = 1.65
    c: Radius(g2) = 1.65
    c: DistanceY(g3,g-1) = 2
    c: DistanceY(g2,g-1) = 2
    c: DistanceY(g-1,g0) = 78
    c: DistanceY(g-1,g1) = 78
    c: DistanceX(g0,g-1) = 0
    c: DistanceX(g-1,g3) = 0
    c: DistanceX(g-1,g2) = 155
    c: DistanceX(g0,g1) = 155
FEATURE [PartDesign::Pocket] Pocket011
  BaseFeature = -> Pad003
  Length = 5
  Length2 = 100
  Profile = -> Sketch016
  Reversed = true
  Type = 1
FEATURE [Part::Feature] Cut001001  label="hex-cut"
  Placement = pos=(70,58,0) rot=(0,0,1;0rad)
  shape: bbox 50 x 14.96 x 10 mm, 92 faces, 12 solids (baked)
FEATURE [Part::Feature] Cut001002  label="hex-cut001"
  Placement = pos=(70,18,0) rot=(0,0,1;3.14159rad)
  shape: bbox 50 x 14.96 x 10 mm, 92 faces, 12 solids (baked)
FEATURE [Part::Feature] Cut001003  label="hex-cut002"
  Placement = pos=(50,38,0) rot=(0,0,1;1.5708rad)
  shape: bbox 14.96 x 50 x 10 mm, 92 faces, 12 solids (baked)
FEATURE [Part::Feature] Cut001004  label="hex-cut003"
  Placement = pos=(90,38,0) rot=(0,0,-1;1.5708rad)
  shape: bbox 14.96 x 50 x 10 mm, 92 faces, 12 solids (baked)
FEATURE [Sketcher::SketchObject] Sketch017
  FullyConstrained = true
  MapMode = 5
  Support = -> [DatumPlane006]
  expr: Constraints[2] = <<args>>.fan_offset
  expr: Constraints[0] = <<args>>.pixel_h / 2
  sketch-geometry (5):
    g0: Circle CenterX=60 CenterY=38 CenterZ=0 NormalX=0 NormalY=0 NormalZ=1 AngleXU=0 Radius=19
    g1: Circle CenterX=44 CenterY=54 CenterZ=0 NormalX=0 NormalY=0 NormalZ=1 AngleXU=0 Radius=1.9
    g2: Circle CenterX=76 CenterY=54 CenterZ=0 NormalX=0 NormalY=0 NormalZ=1 AngleXU=0 Radius=1.9
    g3: Circle CenterX=76 CenterY=22 CenterZ=0 NormalX=0 NormalY=0 NormalZ=1 AngleXU=0 Radius=1.9
    g4: Circle CenterX=44 CenterY=22 CenterZ=0 NormalX=0 NormalY=0 NormalZ=1 AngleXU=0 Radius=1.9
  constraints (15):
    c: DistanceY(g-1,g0) = 38
    c: Radius(g0) = 19
    c: DistanceX(g-1,g0) = 60
    c: Vertical(g4,g1)
    c: Vertical(g2,g3)
    c: Horizontal(g1,g2)
    c: DistanceX(g1,g0) = 16
    c: DistanceX(g1,g2) = 32
    c: DistanceY(g0,g2) = 16
    c: DistanceY(g3,g2) = 32
    c: Horizontal(g4,g3)
    c: Radius(g1) = 1.9
    c: Radius(g2) = 1.9
    c: Radius(g4) = 1.9
    c: Radius(g3) = 1.9
FEATURE [PartDesign::Pocket] Pocket012
  BaseFeature = -> Pocket011
  Length = 5
  Length2 = 100
  Profile = -> Sketch017
  Reversed = true
  Type = 1
FEATURE [Sketcher::SketchObject] Sketch020
  FullyConstrained = true
  MapMode = 5
  Placement = pos=(0,0,8) rot=(0,0,1;0rad)
  Support = -> [DatumPlane007]
  expr: Constraints[9] = <<args>>.pixel_h
  expr: Constraints[8] = <<args>>.pixel_w
  sketch-geometry (4):
    g0: LineSegment StartX=0 StartY=76 StartZ=0 EndX=155 EndY=76 EndZ=0
    g1: LineSegment StartX=155 StartY=76 StartZ=0 EndX=155 EndY=0 EndZ=0
    g2: LineSegment StartX=155 StartY=0 StartZ=0 EndX=0 EndY=0 EndZ=0
    g3: LineSegment StartX=0 StartY=0 StartZ=0 EndX=0 EndY=76 EndZ=0
  constraints (12):
    c: Coincident(g0,g1)
    c: Coincident(g1,g2)
    c: Coincident(g2,g3)
    c: Coincident(g3,g0)
    c: Horizontal(g0)
    c: Horizontal(g2)
    c: Vertical(g1)
    c: Vertical(g3)
    c: DistanceX(g0,g0) = 155
    c: DistanceY(g1,g1) = 76
    c: DistanceX(g-1,g2) = 0
    c: DistanceY(g-1,g2) = 0
FEATURE [PartDesign::Pocket] Pocket015
  BaseFeature = -> Pocket012
  Length = 1
  Length2 = 100
  Profile = -> Sketch020
  Type = 0
FEATURE [Sketcher::SketchObject] Sketch021
  FullyConstrained = true
  MapMode = 5
  Placement = pos=(0,-7,-1.6e-15) rot=(1,0,0;1.5708rad)
  Support = -> [DatumPlane009]
  expr: Constraints[10] = <<args>>.sim_slot_width - 0.3 + 2
  expr: Constraints[9] = <<args>>.sim_slot_offset + 0.15 - 1
  expr: Constraints[8] = <<args>>.back_thickness
  sketch-geometry (4):
    g0: LineSegment StartX=27.15 StartY=9 StartZ=0 EndX=43.85 EndY=9 EndZ=0
    g1: LineSegment StartX=43.85 StartY=9 StartZ=0 EndX=43.85 EndY=8 EndZ=0
    g2: LineSegment StartX=43.85 StartY=8 StartZ=0 EndX=27.15 EndY=8 EndZ=0
    g3: LineSegment StartX=27.15 StartY=8 StartZ=0 EndX=27.15 EndY=9 EndZ=0
  constraints (12):
    c: Coincident(g0,g1)
    c: Coincident(g1,g2)
    c: Coincident(g2,g3)
    c: Coincident(g3,g0)
    c: Horizontal(g0)
    c: Horizontal(g2)
    c: Vertical(g1)
    c: Vertical(g3)
    c: DistanceY(g-1,g2) = 8
    c: DistanceX(g-1,g2) = 27.15
    c: DistanceX(g0,g0) = 16.7
    c: DistanceY(g1,g1) = 1
FEATURE [PartDesign::Pad] Pad004
  BaseFeature = -> Pocket015
  Direction = (1,1,1)
  Length = 7
  Length2 = 100
  Profile = -> Sketch021
  Reversed = true
  Type = 0
  expr: Length = <<args>>.case_heigh_offset
FEATURE [Part::Feature] Body004012  label="din-mount-template"
  Placement = pos=(4,39,-8) rot=(0,0,1;0rad)
  shape: bbox 18 x 63.6 x 7.6 mm, 165 faces (baked)
FEATURE [Part::Feature] Body004013  label="din-mount-template001"
  Placement = pos=(151,39,-8) rot=(0,0,1;0rad)
  shape: bbox 18 x 63.6 x 7.6 mm, 165 faces (baked)
FEATURE [Sketcher::SketchObject] Sketch023
  FullyConstrained = true
  MapMode = 5
  Placement = pos=(0,0,8) rot=(0,0,1;0rad)
  Support = -> [DatumPlane007]
  expr: Constraints[2] = <<args>>.wiring_hole_radius
  expr: Constraints[1] = <<args>>.pixel_h - <<args>>.wiring_hole_radius - 7
  expr: Constraints[0] = <<args>>.wiring_hole_offset
  sketch-geometry (1):
    g0: Circle CenterX=120 CenterY=65 CenterZ=0 NormalX=0 NormalY=0 NormalZ=1 AngleXU=0 Radius=4
  constraints (3):
    c: DistanceX(g-1,g0) = 120
    c: DistanceY(g-1,g0) = 65
    c: Radius(g0) = 4
FEATURE [PartDesign::Pocket] Pocket017
  BaseFeature = -> Pad004
  Length = 5
  Length2 = 100
  Profile = -> Sketch023
  Type = 1
FEATURE [Sketcher::SketchObject] Sketch024
  FullyConstrained = true
  MapMode = 5
  Support = -> [DatumPlane006]
  expr: Constraints[49] = <<args>>.pixel_h - <<args>>.wiring_hole_radius - 20
  expr: Constraints[38] = <<args>>.wiring_hole_offset
  sketch-geometry (20):
    g0: ArcOfCircle CenterX=115 CenterY=57 CenterZ=0 NormalX=0 NormalY=0 NormalZ=1 AngleXU=0 Radius=1.5 StartAngle=6e-16 EndAngle=3.14159
    g1: ArcOfCircle CenterX=115 CenterY=52 CenterZ=0 NormalX=0 NormalY=0 NormalZ=1 AngleXU=0 Radius=1.5 StartAngle=3.14159 EndAngle=6.28319
    g2: LineSegment StartX=113.5 StartY=57 StartZ=0 EndX=113.5 EndY=52 EndZ=0
    g3: LineSegment StartX=116.5 StartY=57 StartZ=0 EndX=116.5 EndY=52 EndZ=0
    g4: ArcOfCircle CenterX=110 CenterY=57 CenterZ=0 NormalX=0 NormalY=0 NormalZ=1 AngleXU=0 Radius=1.5 StartAngle=1.7e-15 EndAngle=3.14159
    g5: ArcOfCircle CenterX=110 CenterY=52 CenterZ=0 NormalX=0 NormalY=0 NormalZ=1 AngleXU=0 Radius=1.5 StartAngle=3.14159 EndAngle=6.28319
    g6: LineSegment StartX=108.5 StartY=57 StartZ=0 EndX=108.5 EndY=52 EndZ=0
    g7: LineSegment StartX=111.5 StartY=57 StartZ=0 EndX=111.5 EndY=52 EndZ=0
    g8: ArcOfCircle CenterX=125 CenterY=57 CenterZ=0 NormalX=0 NormalY=0 NormalZ=1 AngleXU=0 Radius=1.5 StartAngle=1.4e-15 EndAngle=3.14159
    g9: ArcOfCircle CenterX=125 CenterY=52 CenterZ=0 NormalX=0 NormalY=0 NormalZ=1 AngleXU=0 Radius=1.5 StartAngle=3.14159 EndAngle=6.28319
    g10: LineSegment StartX=123.5 StartY=57 StartZ=0 EndX=123.5 EndY=52 EndZ=0
    g11: LineSegment StartX=126.5 StartY=57 StartZ=0 EndX=126.5 EndY=52 EndZ=0
    g12: ArcOfCircle CenterX=130 CenterY=57 CenterZ=0 NormalX=0 NormalY=0 NormalZ=1 AngleXU=0 Radius=1.5 StartAngle=0 EndAngle=3.14159
    g13: ArcOfCircle CenterX=130 CenterY=52 CenterZ=0 NormalX=0 NormalY=0 NormalZ=1 AngleXU=0 Radius=1.5 StartAngle=3.14159 EndAngle=6.28319
    g14: LineSegment StartX=128.5 StartY=57 StartZ=0 EndX=128.5 EndY=52 EndZ=0
    g15: LineSegment StartX=131.5 StartY=57 StartZ=0 EndX=131.5 EndY=52 EndZ=0
    g16: ArcOfCircle CenterX=120 CenterY=57 CenterZ=0 NormalX=0 NormalY=0 NormalZ=1 AngleXU=0 Radius=1.5 StartAngle=6e-16 EndAngle=3.14159
    g17: ArcOfCircle CenterX=120 CenterY=52 CenterZ=0 NormalX=0 NormalY=0 NormalZ=1 AngleXU=0 Radius=1.5 StartAngle=3.14159 EndAngle=6.28319
    g18: LineSegment StartX=118.5 StartY=57 StartZ=0 EndX=118.5 EndY=52 EndZ=0
    g19: LineSegment StartX=121.5 StartY=57 StartZ=0 EndX=121.5 EndY=52 EndZ=0
  constraints (50):
    c: Tangent(g0,g3) = 1.5708
    c: Tangent(g0,g2) = -1.5708
    c: Tangent(g2,g1) = -1.5708
    c: Tangent(g3,g1) = 1.5708
    c: Vertical(g2)
    c: Equal(g0,g1)
    c: Tangent(g4,g7) = 1.5708
    c: Tangent(g4,g6) = -1.5708
    c: Tangent(g6,g5) = -1.5708
    c: Tangent(g7,g5) = 1.5708
    c: Vertical(g6)
    c: Equal(g4,g5)
    c: Tangent(g8,g11) = 1.5708
    c: Tangent(g8,g10) = -1.5708
    c: Tangent(g10,g9) = -1.5708
    c: Tangent(g11,g9) = 1.5708
    c: Vertical(g10)
    c: Equal(g8,g9)
    c: Tangent(g12,g15) = 1.5708
    c: Tangent(g12,g14) = -1.5708
    c: Tangent(g14,g13) = -1.5708
    c: Tangent(g15,g13) = 1.5708
    c: Vertical(g14)
    c: Equal(g12,g13)
    c: Tangent(g16,g19) = 1.5708
    c: Tangent(g16,g18) = -1.5708
    c: Tangent(g18,g17) = -1.5708
    c: Tangent(g19,g17) = 1.5708
    c: Vertical(g18)
    c: Equal(g16,g17)
    c: Horizontal(g4,g0)
    c: Horizontal(g0,g16)
    c: Horizontal(g16,g8)
    c: Horizontal(g8,g12)
    c: Horizontal(g5,g1)
    c: Horizontal(g1,g17)
    c: Horizontal(g17,g9)
    c: Horizontal(g9,g13)
    c: DistanceX(g-1,g17) = 120
    c: Radius(g4) = 1.5
    c: Radius(g0) = 1.5
    c: Radius(g12) = 1.5
    c: Radius(g8) = 1.5
    c: Radius(g16) = 1.5
    c: DistanceX(g16,g8) = 5
    c: DistanceX(g8,g12) = 5
    c: DistanceX(g0,g16) = 5
    c: DistanceX(g4,g0) = 5
    c: DistanceY(g13,g12) = 5
    c: DistanceY(g-1,g5) = 52
FEATURE [PartDesign::Pad] Pad005
  BaseFeature = -> Pocket017
  Direction = (1,1,1)
  Length = 7
  Length2 = 100
  Profile = -> Sketch024
  Type = 0
  expr: Length = <<args>>.back_thickness - 1
FEATURE [Sketcher::SketchObject] Sketch005
  AttachmentOffset = pos=(0,0,-10) rot=(0,0,1;0rad)
  FullyConstrained = true
  MapMode = 5
  Support = -> [Pocket002]
  expr: Constraints[11] = <<args>>.button_volume_offset + <<args>>.button_volume_width + 2
  expr: .AttachmentOffset.Base.z = -<<args>>.case_thickness
  expr: Constraints[10] = <<args>>.pixel_h - <<args>>.screen_side_offset
  expr: Constraints[9] = <<args>>.button_power_offset - 2
  sketch-geometry (4):
    g0: LineSegment StartX=35 StartY=78 StartZ=0 EndX=81 EndY=78 EndZ=0
    g1: LineSegment StartX=81 StartY=78 StartZ=0 EndX=81 EndY=72.5 EndZ=0
    g2: LineSegment StartX=81 StartY=72.5 StartZ=0 EndX=35 EndY=72.5 EndZ=0
    g3: LineSegment StartX=35 StartY=72.5 StartZ=0 EndX=35 EndY=78 EndZ=0
  constraints (12):
    c: Coincident(g0,g1)
    c: Coincident(g1,g2)
    c: Coincident(g2,g3)
    c: Coincident(g3,g0)
    c: Horizontal(g0)
    c: Horizontal(g2)
    c: Vertical(g1)
    c: Vertical(g3)
    c: DistanceY(g1,g1) = 5.5
    c: DistanceX(g-1,g2) = 35
    c: DistanceY(g-1,g2) = 72.5
    c: DistanceX(g-1,g1) = 81
FEATURE [PartDesign::Pocket] Pocket003
  BaseFeature = -> Pocket002
  Length = 8
  Length2 = 100
  Profile = -> Sketch005
  Reversed = true
  Type = 0
FEATURE [PartDesign::Pocket] Pocket005  label="right-pocket"
  BaseFeature = -> Pocket003
  Length = 7
  Length2 = 100
  Profile = -> Sketch007
  Reversed = true
  Type = 0
  expr: Length = <<args>>.case_heigh_offset
FEATURE [PartDesign::Pocket] Pocket006  label="bottom-pocket"
  BaseFeature = -> Pocket005
  Length = 5
  Length2 = 100
  Profile = -> Sketch008
  Type = 0
  expr: Length = <<args>>.case_width_offset
FEATURE [PartDesign::Pocket] Pocket007  label="left-pocket"
  BaseFeature = -> Pocket006
  Length = 7
  Length2 = 100
  Profile = -> Sketch009
  Type = 0
  expr: Length = <<args>>.case_heigh_offset
FEATURE [PartDesign::Pocket] Pocket008  label="top-pocket"
  BaseFeature = -> Pocket007
  Length = 7
  Length2 = 100
  Profile = -> Sketch010
  Reversed = true
  Type = 0
  expr: Length = <<args>>.case_heigh_offset
FEATURE [PartDesign::Pocket] Pocket010  label="corner-bolt"
  BaseFeature = -> Pocket008
  Length = 8
  Length2 = 100
  Profile = -> Sketch015
  Reversed = true
  Type = 0
  expr: Length = <<args>>.case_thickness - 2
FEATURE [PartDesign::Fillet] Fillet004
  Base = -> Pocket010 [Edge58,Edge163,Edge60,Edge72]
  BaseFeature = -> Pocket010
  Radius = 8.5
  SupportTransform = false
  expr: Radius = <<args>>.pixel_corner_radius
FEATURE [PartDesign::Chamfer] Chamfer003
  Angle = 45
  Base = -> Fillet004 [Edge27,Edge25,Edge33,Edge103]
  BaseFeature = -> Fillet004
  ChamferType = 0
  FlipDirection = false
  Size = 3
  Size2 = 1
  SupportTransform = false
  expr: Size = <<args>>.case_corner_radius
FEATURE [PartDesign::Chamfer] Chamfer004
  Angle = 45
  Base = -> Chamfer003 [Edge65,Edge66,Edge63,Edge64,Edge59,Edge60,Edge62,Edge61,Edge58,Edge67,Edge68,Edge70,Edge69]
  BaseFeature = -> Chamfer003
  ChamferType = 1
  FlipDirection = false
  Size = 0.5
  Size2 = 1.6
  SupportTransform = false
FEATURE [PartDesign::Fillet] Fillet005
  Base = -> Chamfer004 [Edge38,Edge31,Edge42,Edge58,Edge34,Edge40,Edge50,Edge60]
  BaseFeature = -> Chamfer004
  Radius = 2
  SupportTransform = false
FEATURE [PartDesign::Chamfer] Chamfer005
  Angle = 45
  Base = -> Fillet005 [Edge3,Edge5,Edge7,Edge9,Edge11,Edge13,Edge15,Edge16,Edge14,Edge12,Edge10,Edge8,Edge6,Edge4,Edge2,Edge1]
  BaseFeature = -> Fillet005
  ChamferType = 1
  FlipDirection = false
  Size = 1
  Size2 = 1.5
  SupportTransform = false
FEATURE [PartDesign::Fillet] Fillet006
  Base = -> Pad005 [Edge101,Edge107,Edge109,Edge102]
  BaseFeature = -> Pad005
  Radius = 8.5
  SupportTransform = false
  expr: Radius = <<args>>.pixel_corner_radius
FEATURE [PartDesign::Chamfer] Chamfer006
  Angle = 45
  Base = -> Fillet006 [Edge28,Edge36,Edge42,Edge27]
  BaseFeature = -> Fillet006
  ChamferType = 0
  FlipDirection = false
  Size = 3
  Size2 = 1
  SupportTransform = false
  expr: Size = <<args>>.case_corner_radius
FEATURE [PartDesign::Fillet] Fillet007
  Base = -> Chamfer006 [Edge28,Edge37,Edge41,Edge119,Edge90,Edge16,Edge17,Edge23]
  BaseFeature = -> Chamfer006
  Radius = 2
  SupportTransform = false
FEATURE [PartDesign::Chamfer] Chamfer007
  Angle = 45
  Base = -> Fillet007 [Edge19,Edge26,Edge31,Edge40,Edge44,Edge69,Edge48,Edge67,Edge52,Edge58,Edge63,Edge71,Edge72,Edge73,Edge74,Edge80,Edge77,Edge76,Edge75,Edge105]
  BaseFeature = -> Fillet007
  ChamferType = 0
  FlipDirection = false
  Size = 0.4
  Size2 = 1
  SupportTransform = false
FEATURE [Part::MultiFuse] Fusion
  Shapes = -> [Cut001001,Cut001002,Cut001003,Cut001004]
FEATURE [Part::Box] Box  label="Cube"
  AttacherType = Attacher::AttachEngine3D
  Height = 10
  Length = 50
  Placement = pos=(45,0,2) rot=(0,0,1;0rad)
  Width = 6
FEATURE [Part::Box] Box001  label="Cube001"
  AttacherType = Attacher::AttachEngine3D
  Height = 10
  Length = 50
  Placement = pos=(45,70,2) rot=(0,0,1;0rad)
  Width = 6
FEATURE [Part::MultiFuse] Fusion002
  Shapes = -> [Box,Box001]
FEATURE [Part::Cut] Cut001005  label="fan-air-channel"
  Base = -> Fusion
  Placement = pos=(-10,0,-8) rot=(0,0,1;0rad)
  Tool = -> Fusion002
FEATURE [Sketcher::SketchObject] Sketch025
  FullyConstrained = true
  MapMode = 5
  Support = -> [DatumPlane006]
  expr: Constraints[2] = <<args>>.pixel_h / 2
  expr: Constraints[0] = <<args>>.fan_offset
  sketch-geometry (12):
    g0: ArcOfCircle CenterX=60 CenterY=38 CenterZ=0 NormalX=0 NormalY=0 NormalZ=1 AngleXU=0 Radius=19 StartAngle=3.84567 EndAngle=4.00832
    g1: ArcOfCircle CenterX=44 CenterY=54 CenterZ=0 NormalX=0 NormalY=0 NormalZ=1 AngleXU=0 Radius=4 StartAngle=5.89394 EndAngle=11.3848
    g2: Circle CenterX=44 CenterY=54 CenterZ=0 NormalX=0 NormalY=0 NormalZ=1 AngleXU=0 Radius=1.9
    g3: Circle CenterX=76 CenterY=54 CenterZ=0 NormalX=0 NormalY=0 NormalZ=1 AngleXU=0 Radius=1.9
    g4: ArcOfCircle CenterX=76 CenterY=54 CenterZ=0 NormalX=0 NormalY=0 NormalZ=1 AngleXU=0 Radius=4 StartAngle=4.32314 EndAngle=9.81403
    g5: Circle CenterX=44 CenterY=22 CenterZ=0 NormalX=0 NormalY=0 NormalZ=1 AngleXU=0 Radius=1.9
    g6: ArcOfCircle CenterX=44 CenterY=22 CenterZ=0 NormalX=0 NormalY=0 NormalZ=1 AngleXU=0 Radius=4 StartAngle=1.18155 EndAngle=6.67243
    g7: Circle CenterX=76 CenterY=22 CenterZ=0 NormalX=0 NormalY=0 NormalZ=1 AngleXU=0 Radius=1.9
    g8: ArcOfCircle CenterX=76 CenterY=22 CenterZ=0 NormalX=0 NormalY=0 NormalZ=1 AngleXU=0 Radius=4 StartAngle=2.75234 EndAngle=8.24323
    g9: ArcOfCircle CenterX=60 CenterY=38 CenterZ=0 NormalX=0 NormalY=0 NormalZ=1 AngleXU=0 Radius=19 StartAngle=2.27487 EndAngle=2.43752
    g10: ArcOfCircle CenterX=60 CenterY=38 CenterZ=0 NormalX=0 NormalY=0 NormalZ=1 AngleXU=0 Radius=19 StartAngle=0.704073 EndAngle=0.866723
    g11: ArcOfCircle CenterX=60 CenterY=38 CenterZ=0 NormalX=0 NormalY=0 NormalZ=1 AngleXU=0 Radius=19 StartAngle=5.41646 EndAngle=5.57911
  constraints (37):
    c: DistanceX(g-1,g0) = 60
    c: Radius(g0) = 19
    c: DistanceY(g-1,g0) = 38
    c: Coincident(g2,g1)
    c: Coincident(g4,g3)
    c: Coincident(g6,g5)
    c: Coincident(g8,g7)
    c: Radius(g2) = 1.9
    c: Radius(g5) = 1.9
    c: Radius(g3) = 1.9
    c: Radius(g7) = 1.9
    c: Horizontal(g1,g3)
    c: Horizontal(g5,g7)
    c: Vertical(g5,g1)
    c: Vertical(g3,g7)
    c: DistanceX(g1,g0) = 16
    c: DistanceX(g0,g3) = 16
    c: DistanceY(g5,g0) = 16
    c: DistanceY(g0,g3) = 16
    c: Radius(g1) = 4
    c: Radius(g4) = 4
    c: Radius(g8) = 4
    c: Radius(g6) = 4
    c: Equal(g0,g9)
    c: Coincident(g0,g9)
    c: Equal(g0,g10)
    c: Coincident(g0,g10)
    c: Equal(g0,g11)
    c: Coincident(g0,g11)
    c: Coincident(g8,g11)
    c: Coincident(g8,g11)
    c: Coincident(g6,g0)
    c: Coincident(g6,g0)
    c: Coincident(g1,g9)
    c: Coincident(g1,g9)
    c: Coincident(g4,g10)
    c: Coincident(g4,g10)
FEATURE [PartDesign::Pad] Pad006
  BaseFeature = -> Chamfer007
  Direction = (1,1,1)
  Length = 6
  Length2 = 100
  Profile = -> Sketch025
  Type = 0
  expr: Length = <<args>>.back_thickness - 2
FEATURE [PartDesign::Chamfer] Chamfer008
  Angle = 45
  Base = -> Pad006 [Edge215,Edge102]
  BaseFeature = -> Pad006
  ChamferType = 0
  FlipDirection = false
  Refine = true
  Size = 1
  Size2 = 1
  SupportTransform = false
FEATURE [Sketcher::SketchObject] Sketch026
  FullyConstrained = true
  MapMode = 5
  Placement = pos=(160,-3.55e-14,3.55e-14) rot=(0.57735,0.57735,0.57735;2.0944rad)
  Support = -> [DatumPlane003]
  expr: Constraints[1] = <<args>>.pixel_h
  sketch-geometry (5):
    g0: GeomPoint X=76 Y=0 Z=0
    g1: Circle CenterX=5 CenterY=4 CenterZ=0 NormalX=0 NormalY=0 NormalZ=1 AngleXU=0 Radius=1.9
    g2: Circle CenterX=71 CenterY=4 CenterZ=0 NormalX=0 NormalY=0 NormalZ=1 AngleXU=0 Radius=1.9
    g3: Circle CenterX=32 CenterY=4 CenterZ=0 NormalX=0 NormalY=0 NormalZ=1 AngleXU=0 Radius=1.9
    g4: Circle CenterX=44 CenterY=4 CenterZ=0 NormalX=0 NormalY=0 NormalZ=1 AngleXU=0 Radius=1.9
  constraints (14):
    c: PointOnObject(g0,g-1)
    c: DistanceX(g-1,g0) = 76
    c: Horizontal(g1,g3)
    c: Horizontal(g3,g4)
    c: Horizontal(g4,g2)
    c: DistanceY(g-1,g1) = 4
    c: Radius(g1) = 1.9
    c: Radius(g3) = 1.9
    c: Radius(g4) = 1.9
    c: Radius(g2) = 1.9
    c: DistanceX(g-1,g1) = 5
    c: DistanceX(g2,g0) = 5
    c: DistanceX(g1,g3) = 27
    c: DistanceX(g4,g2) = 27
FEATURE [PartDesign::Pocket] Pocket018
  BaseFeature = -> Chamfer005
  Length = 5
  Length2 = 100
  Profile = -> Sketch026
  Type = 1
FEATURE [Sketcher::SketchObject] Sketch027
  FullyConstrained = true
  MapMode = 5
  Placement = pos=(0,-7,-1.6e-15) rot=(1,0,0;1.5708rad)
  Support = -> [DatumPlane004]
  expr: Constraints[9] = <<args>>.pixel_w
  sketch-geometry (5):
    g0: Circle CenterX=20 CenterY=4 CenterZ=0 NormalX=0 NormalY=0 NormalZ=1 AngleXU=0 Radius=1.9
    g1: Circle CenterX=135 CenterY=4 CenterZ=0 NormalX=0 NormalY=0 NormalZ=1 AngleXU=0 Radius=1.9
    g2: Circle CenterX=90 CenterY=4 CenterZ=0 NormalX=0 NormalY=0 NormalZ=1 AngleXU=0 Radius=1.9
    g3: Circle CenterX=65 CenterY=4 CenterZ=0 NormalX=0 NormalY=0 NormalZ=1 AngleXU=0 Radius=1.9
    g4: GeomPoint X=155 Y=0 Z=0
  constraints (14):
    c: Horizontal(g0,g3)
    c: Horizontal(g3,g2)
    c: Horizontal(g2,g1)
    c: DistanceY(g-1,g0) = 4
    c: Radius(g0) = 1.9
    c: Radius(g3) = 1.9
    c: Radius(g2) = 1.9
    c: Radius(g1) = 1.9
    c: PointOnObject(g4,g-1)
    c: DistanceX(g-1,g4) = 155
    c: DistanceX(g-1,g0) = 20
    c: DistanceX(g1,g4) = 20
    c: DistanceX(g2,g1) = 45
    c: DistanceX(g0,g3) = 45
FEATURE [PartDesign::Pocket] Pocket019
  BaseFeature = -> Pocket018
  Length = 5
  Length2 = 100
  Profile = -> Sketch027
  Type = 1
FEATURE [Sketcher::SketchObject] Sketch028
  FullyConstrained = true
  MapMode = 5
  Placement = pos=(0,-7,-1.6e-15) rot=(1,0,0;1.5708rad)
  Support = -> [DatumPlane009]
  expr: Constraints[1] = <<args>>.pixel_w
  sketch-geometry (5):
    g0: Circle CenterX=20 CenterY=4 CenterZ=0 NormalX=0 NormalY=0 NormalZ=1 AngleXU=0 Radius=1.9
    g1: Circle CenterX=65 CenterY=4 CenterZ=0 NormalX=0 NormalY=0 NormalZ=1 AngleXU=0 Radius=1.9
    g2: Circle CenterX=90 CenterY=4 CenterZ=0 NormalX=0 NormalY=0 NormalZ=1 AngleXU=0 Radius=1.9
    g3: Circle CenterX=135 CenterY=4 CenterZ=0 NormalX=0 NormalY=0 NormalZ=1 AngleXU=0 Radius=1.9
    g4: GeomPoint X=155 Y=0 Z=0
  constraints (14):
    c: PointOnObject(g4,g-1)
    c: DistanceX(g-1,g4) = 155
    c: DistanceX(g-1,g0) = 20
    c: DistanceX(g0,g1) = 45
    c: DistanceX(g2,g3) = 45
    c: DistanceX(g3,g4) = 20
    c: Horizontal(g0,g1)
    c: Horizontal(g1,g2)
    c: Horizontal(g2,g3)
    c: DistanceY(g-1,g0) = 4
    c: Radius(g0) = 1.9
    c: Radius(g1) = 1.9
    c: Radius(g2) = 1.9
    c: Radius(g3) = 1.9
FEATURE [PartDesign::Pocket] Pocket020
  BaseFeature = -> Chamfer008
  Length = 10
  Length2 = 100
  Profile = -> Sketch028
  Type = 0
FEATURE [Sketcher::SketchObject] Sketch029
  FullyConstrained = true
  MapMode = 5
  Placement = pos=(0,83,1.84e-14) rot=(1,0,0;1.5708rad)
  Support = -> [DatumPlane012]
  expr: Constraints[1] = <<args>>.pixel_w
  sketch-geometry (4):
    g0: GeomPoint X=155 Y=0 Z=0
    g1: Circle CenterX=20 CenterY=4 CenterZ=0 NormalX=0 NormalY=0 NormalZ=1 AngleXU=0 Radius=1.9
    g2: Circle CenterX=135 CenterY=4 CenterZ=0 NormalX=0 NormalY=0 NormalZ=1 AngleXU=0 Radius=1.9
    g3: Circle CenterX=90 CenterY=4 CenterZ=0 NormalX=0 NormalY=0 NormalZ=1 AngleXU=0 Radius=1.9
  constraints (11):
    c: PointOnObject(g0,g-1)
    c: DistanceX(g-1,g0) = 155
    c: Horizontal(g3,g1)
    c: Horizontal(g1,g2)
    c: DistanceY(g-1,g1) = 4
    c: DistanceX(g-1,g1) = 20
    c: DistanceX(g2,g0) = 20
    c: DistanceX(g3,g2) = 45
    c: Radius(g1) = 1.9
    c: Radius(g3) = 1.9
    c: Radius(g2) = 1.9
FEATURE [PartDesign::Pocket] Pocket021
  BaseFeature = -> Pocket020
  Length = 10
  Length2 = 100
  Profile = -> Sketch029
  Reversed = true
  Type = 0
FEATURE [Sketcher::SketchObject] Sketch030
  FullyConstrained = true
  MapMode = 5
  Placement = pos=(160,-3.55e-14,3.55e-14) rot=(0.57735,0.57735,0.57735;2.0944rad)
  Support = -> [DatumPlane011]
  expr: Constraints[1] = <<args>>.pixel_h
  sketch-geometry (5):
    g0: Circle CenterX=5 CenterY=4 CenterZ=0 NormalX=0 NormalY=0 NormalZ=1 AngleXU=0 Radius=1.9
    g1: Circle CenterX=32 CenterY=4 CenterZ=0 NormalX=0 NormalY=0 NormalZ=1 AngleXU=0 Radius=1.9
    g2: Circle CenterX=44 CenterY=4 CenterZ=0 NormalX=0 NormalY=0 NormalZ=1 AngleXU=0 Radius=1.9
    g3: Circle CenterX=71 CenterY=4 CenterZ=0 NormalX=0 NormalY=0 NormalZ=1 AngleXU=0 Radius=1.9
    g4: GeomPoint X=76 Y=0 Z=0
  constraints (14):
    c: PointOnObject(g4,g-1)
    c: DistanceX(g-1,g4) = 76
    c: Horizontal(g0,g1)
    c: Horizontal(g1,g2)
    c: Horizontal(g2,g3)
    c: DistanceY(g-1,g0) = 4
    c: DistanceX(g-1,g0) = 5
    c: DistanceX(g3,g4) = 5
    c: DistanceX(g2,g3) = 27
    c: DistanceX(g0,g1) = 27
    c: Radius(g0) = 1.9
    c: Radius(g1) = 1.9
    c: Radius(g2) = 1.9
    c: Radius(g3) = 1.9
FEATURE [PartDesign::Pocket] Pocket022
  BaseFeature = -> Pocket021
  Length = 10
  Length2 = 100
  Profile = -> Sketch030
  Type = 0
FEATURE [Sketcher::SketchObject] Sketch031
  FullyConstrained = true
  MapMode = 5
  Placement = pos=(-5,1.1e-15,-1.1e-15) rot=(0.57735,0.57735,0.57735;2.0944rad)
  Support = -> [DatumPlane010]
  expr: Constraints[1] = <<args>>.pixel_h
  sketch-geometry (5):
    g0: GeomPoint X=76 Y=0 Z=0
    g1: Circle CenterX=5 CenterY=4 CenterZ=0 NormalX=0 NormalY=0 NormalZ=1 AngleXU=0 Radius=1.9
    g2: Circle CenterX=32 CenterY=4 CenterZ=0 NormalX=0 NormalY=0 NormalZ=1 AngleXU=0 Radius=1.9
    g3: Circle CenterX=44 CenterY=4 CenterZ=0 NormalX=0 NormalY=0 NormalZ=1 AngleXU=0 Radius=1.9
    g4: Circle CenterX=71 CenterY=4 CenterZ=0 NormalX=0 NormalY=0 NormalZ=1 AngleXU=0 Radius=1.9
  constraints (14):
    c: PointOnObject(g0,g-1)
    c: DistanceX(g-1,g0) = 76
    c: Horizontal(g1,g2)
    c: Horizontal(g2,g3)
    c: Horizontal(g3,g4)
    c: DistanceY(g-1,g1) = 4
    c: DistanceX(g-1,g1) = 5
    c: DistanceX(g4,g0) = 5
    c: DistanceX(g3,g4) = 27
    c: DistanceX(g1,g2) = 27
    c: Radius(g4) = 1.9
    c: Radius(g3) = 1.9
    c: Radius(g2) = 1.9
    c: Radius(g1) = 1.9
FEATURE [PartDesign::Pocket] Pocket023
  BaseFeature = -> Pocket022
  Length = 10
  Length2 = 100
  Profile = -> Sketch031
  Reversed = true
  Type = 0
FEATURE [PartDesign::Chamfer] Chamfer
  Angle = 45
  Base = -> Pocket023 [Edge159,Edge156,Edge157,Edge158,Edge180,Edge181,Edge182,Edge183,Edge136,Edge135,Edge134,Edge133,Edge20,Edge19,Edge18]
  BaseFeature = -> Pocket023
  ChamferType = 0
  FlipDirection = false
  Size = 0.4
  Size2 = 1
  SupportTransform = false
FEATURE [PartDesign::Chamfer] Chamfer009
  Angle = 45
  Base = -> Pocket019 [Edge155,Edge156,Edge157,Edge135,Edge136,Edge133,Edge134,Edge97,Edge98,Edge99,Edge100,Edge119,Edge120,Edge121,Edge122]
  BaseFeature = -> Pocket019
  ChamferType = 0
  FlipDirection = false
  Size = 0.4
  Size2 = 1
  SupportTransform = false
FEATURE [PartDesign::Chamfer] Chamfer010
  Angle = 45
  Base = -> Chamfer [Edge106,Edge105,Edge104,Edge103]
  BaseFeature = -> Chamfer
  ChamferType = 0
  FlipDirection = false
  Size = 0.4
  Size2 = 1
  SupportTransform = false
FEATURE [Part::Box] Box002  label="Cube002"
  AttacherType = Attacher::AttachEngine3D
  Height = 5.5
  Length = 12
  Placement = pos=(36,75,1.25) rot=(0,0,1;0rad)
  Width = 1
FEATURE [Part::Box] Box003  label="Cube003"
  AttacherType = Attacher::AttachEngine3D
  Height = 5.5
  Length = 9.5
  Placement = pos=(37.25,76,1.25) rot=(0,0,1;0rad)
  Width = 11
FEATURE [Part::Box] Box004  label="Cube004"
  AttacherType = Attacher::AttachEngine3D
  Height = 5.5
  Length = 8
  Placement = pos=(70.75,76,1.25) rot=(0,0,1;0rad)
  Width = 11
FEATURE [Part::Box] Box005  label="Cube005"
  AttacherType = Attacher::AttachEngine3D
  Height = 5.5
  Length = 9.25
  Placement = pos=(58,75,1.25) rot=(0,0,1;0rad)
  Width = 1
FEATURE [Part::Box] Box006  label="Cube006"
  AttacherType = Attacher::AttachEngine3D
  Height = 5.5
  Length = 8
  Placement = pos=(59.25,76,1.25) rot=(0,0,1;0rad)
  Width = 11
FEATURE [Part::Box] Box007  label="Cube007"
  AttacherType = Attacher::AttachEngine3D
  Height = 5.5
  Length = 9.25
  Placement = pos=(70.75,75,1.25) rot=(0,0,1;0rad)
  Width = 1
FEATURE [Part::Box] Box008  label="Cube008"
  AttacherType = Attacher::AttachEngine3D
  Height = 5.5
  Length = 3.5
  Placement = pos=(67.25,79,1.25) rot=(0,0,1;0rad)
  Width = 2
FEATURE [Part::FeaturePython] Tube  # WARN: FeaturePython — macro-defined, semantics opaque (R4)
  AttacherType = Attacher::AttachEngine3D
  Height = 5.5
  InnerRadius = 1
  OuterRadius = 1.75
  Placement = pos=(69,81,1.25) rot=(0,0,1;0rad)
FEATURE [Part::Box] Box009  label="Cube009"
  AttacherType = Attacher::AttachEngine3D
  Height = 5.5
  Length = 1.75
  Placement = pos=(66.25,80,1.25) rot=(0,0,1;0rad)
  Width = 1
FEATURE [Part::Cut] Cut
  Base = -> Tube
  Tool = -> Box008
FEATURE [Part::Box] Box010  label="Cube010"
  AttacherType = Attacher::AttachEngine3D
  Height = 5.5
  Length = 1.75
  Placement = pos=(70,80,1.25) rot=(0,0,1;0rad)
  Width = 1
FEATURE [Part::Box] Box011  label="Cube011"
  AttacherType = Attacher::AttachEngine3D
  Height = 5.5
  Length = 4
  Placement = pos=(60,74.5,1.25) rot=(0,0,1;0rad)
  Width = 1
FEATURE [Part::Box] Box012  label="Cube012"
  AttacherType = Attacher::AttachEngine3D
  Height = 5.5
  Length = 4
  Placement = pos=(74,74.5,1.25) rot=(0,0,1;0rad)
  Width = 1
FEATURE [Part::MultiFuse] Fusion004
  Refine = true
  Shapes = -> [Box012,Box011,Box010,Cut,Box009,Box007,Box006,Box005,Box004]
FEATURE [Part::Box] Box013  label="Cube013"
  AttacherType = Attacher::AttachEngine3D
  Height = 5.5
  Length = 8
  Placement = pos=(38,74.5,1.25) rot=(0,0,1;0rad)
  Width = 1
FEATURE [Part::MultiFuse] Fusion005
  Refine = true
  Shapes = -> [Box013,Box002,Box003]
FEATURE [Part::Chamfer] Chamfer011
  Base = -> Fusion005
  Edges = 2 edges r=0.4: [Edge4,Edge9]
FEATURE [Part::Chamfer] Chamfer012
  Base = -> Fusion004
  Edges = 6 edges r=0.4: [Edge7,Edge10,Edge21,Edge26,Edge74,Edge79]
FEATURE [Part::Chamfer] Chamfer013
  Base = -> Chamfer012
  Edges = 2 edges r=2: [Edge41,Edge76]
FEATURE [Part::Chamfer] Chamfer014  label="power-btn"
  Base = -> Chamfer011
  Edges = 2 edges r=1: [Edge38,Edge40]
  Placement = pos=(0,2,0) rot=(0,0,1;0rad)
FEATURE [Part::Chamfer] Chamfer015  label="volume-btn"
  Base = -> Chamfer013
  Edges = 4 edges r=1: [Edge74,Edge79,Edge90,Edge95]
  Placement = pos=(0,2,0) rot=(0,0,1;0rad)
FEATURE [Sketcher::SketchObject] Sketch032
  FullyConstrained = true
  MapMode = 5
  Support = -> [XY_Plane002]
  expr: Constraints[22] = <<args>>.case_width_offset * 2 + <<args>>.pixel_w + 0.3
  expr: Constraints[21] = <<args>>.case_width_offset + 0.15
  expr: Constraints[20] = <<args>>.case_heigh_offset + 0.15
  sketch-geometry (8):
    g0: LineSegment StartX=-7.15 StartY=17 StartZ=0 EndX=-5.15 EndY=17 EndZ=0
    g1: LineSegment StartX=-5.15 StartY=17 StartZ=0 EndX=-5.15 EndY=-7.15 EndZ=0
    g2: LineSegment StartX=-5.15 StartY=-7.15 StartZ=0 EndX=160.15 EndY=-7.15 EndZ=0
    g3: LineSegment StartX=160.15 StartY=-7.15 StartZ=0 EndX=160.15 EndY=12 EndZ=0
    g4: LineSegment StartX=160.15 StartY=12 StartZ=0 EndX=162.15 EndY=12 EndZ=0
    g5: LineSegment StartX=162.15 StartY=12 StartZ=0 EndX=162.15 EndY=-9.15 EndZ=0
    g6: LineSegment StartX=162.15 StartY=-9.15 StartZ=0 EndX=-7.15 EndY=-9.15 EndZ=0
    g7: LineSegment StartX=-7.15 StartY=-9.15 StartZ=0 EndX=-7.15 EndY=17 EndZ=0
  constraints (24):
    c: Horizontal(g0)
    c: Coincident(g0,g1)
    c: Vertical(g1)
    c: Coincident(g1,g2)
    c: Horizontal(g2)
    c: Coincident(g2,g3)
    c: Vertical(g3)
    c: Coincident(g3,g4)
    c: Horizontal(g4)
    c: Coincident(g4,g5)
    c: Vertical(g5)
    c: Coincident(g5,g6)
    c: Horizontal(g6)
    c: Coincident(g6,g7)
    c: Coincident(g7,g0)
    c: Vertical(g7)
    c: DistanceX(g0,g0) = 2
    c: DistanceX(g4,g4) = 2
    c: DistanceY(g6,g1) = 2
    c: DistanceY(g-1,g0) = 17
    c: DistanceY(g1,g-1) = 7.15
    c: DistanceX(g0,g-1) = 5.15
    c: DistanceX(g2,g2) = 165.3
    c: DistanceY(g-1,g3) = 12
FEATURE [PartDesign::Pad] Pad007
  Direction = (1,1,1)
  Length = 16
  Length2 = 100
  Profile = -> Sketch032
  Type = 0
FEATURE [PartDesign::Chamfer] Chamfer016
  Angle = 45
  Base = -> Pad007 [Edge8,Edge5]
  BaseFeature = -> Pad007
  ChamferType = 0
  FlipDirection = false
  Size = 3
  Size2 = 1
  SupportTransform = false
FEATURE [PartDesign::Fillet] Fillet
  Base = -> Chamfer016 [Edge2,Edge14,Edge25,Edge27]
  BaseFeature = -> Chamfer016
  Radius = 2
  SupportTransform = false
FEATURE [PartDesign::Chamfer] Chamfer017
  Angle = 45
  Base = -> Fillet [Edge34,Edge36]
  BaseFeature = -> Fillet
  ChamferType = 0
  FlipDirection = false
  Size = 3.5
  Size2 = 1
  SupportTransform = false
FEATURE [PartDesign::Fillet] Fillet008
  Base = -> Chamfer017 [Edge17,Edge20,Edge24,Edge28]
  BaseFeature = -> Chamfer017
  Radius = 2
  SupportTransform = false
FEATURE [PartDesign::Chamfer] Chamfer018
  Angle = 45
  Base = -> Fillet008 [Edge3,Edge27,Edge18,Edge57]
  BaseFeature = -> Fillet008
  ChamferType = 0
  FlipDirection = false
  Size = 1
  Size2 = 1
  SupportTransform = false
FEATURE [PartDesign::Chamfer] Chamfer019
  Angle = 45
  Base = -> Chamfer018 [Edge24,Edge25,Edge23,Edge21,Edge1,Edge3,Edge5,Edge7,Edge9,Edge29,Edge35,Edge39,Edge43,Edge47,Edge51,Edge55,Edge60,Edge11,Edge13,Edge15,Edge17,Edge58,Edge59,Edge61,Edge68,Edge66,Edge64,Edge20,Edge18,Edge16,Edge14,Edge12,Edge10,Edge8,Edge6,Edge4,Edge27,Edge31,Edge33,Edge32,+8 more]
  BaseFeature = -> Chamfer018
  ChamferType = 0
  FlipDirection = false
  Size = 0.4
  Size2 = 1
  SupportTransform = false
FEATURE [Sketcher::SketchObject] Sketch033
  FullyConstrained = true
  MapMode = 5
  Placement = pos=(0,-9.15,0) rot=(1,0,0;1.5708rad)
  Support = -> [Chamfer019]
  expr: Constraints[14] = <<args>>.pixel_w
  sketch-geometry (9):
    g0: Circle CenterX=20 CenterY=12 CenterZ=0 NormalX=0 NormalY=0 NormalZ=1 AngleXU=0 Radius=1.65
    g1: Circle CenterX=20 CenterY=4 CenterZ=0 NormalX=0 NormalY=0 NormalZ=1 AngleXU=0 Radius=1.65
    g2: Circle CenterX=65 CenterY=12 CenterZ=0 NormalX=0 NormalY=0 NormalZ=1 AngleXU=0 Radius=1.65
    g3: Circle CenterX=65 CenterY=4 CenterZ=0 NormalX=0 NormalY=0 NormalZ=1 AngleXU=0 Radius=1.65
    g4: Circle CenterX=90 CenterY=12 CenterZ=0 NormalX=0 NormalY=0 NormalZ=1 AngleXU=0 Radius=1.65
    g5: Circle CenterX=90 CenterY=4 CenterZ=0 NormalX=0 NormalY=0 NormalZ=1 AngleXU=0 Radius=1.65
    g6: Circle CenterX=135 CenterY=12 CenterZ=0 NormalX=0 NormalY=0 NormalZ=1 AngleXU=0 Radius=1.65
    g7: Circle CenterX=135 CenterY=4 CenterZ=0 NormalX=0 NormalY=0 NormalZ=1 AngleXU=0 Radius=1.65
    g8: GeomPoint X=155 Y=0 Z=0
  constraints (26):
    c: Horizontal(g0,g2)
    c: Horizontal(g2,g4)
    c: Horizontal(g4,g6)
    c: Horizontal(g1,g3)
    c: Horizontal(g3,g5)
    c: Horizontal(g5,g7)
    c: DistanceY(g-1,g1) = 4
    c: DistanceY(g1,g0) = 8
    c: DistanceX(g-1,g1) = 20
    c: Vertical(g0,g1)
    c: Vertical(g2,g3)
    c: Vertical(g4,g5)
    c: Vertical(g6,g7)
    c: PointOnObject(g8,g-1)
    c: DistanceX(g-1,g8) = 155
    c: DistanceX(g1,g3) = 45
    c: DistanceX(g7,g8) = 20
    c: DistanceX(g5,g7) = 45
    c: Radius(g0) = 1.65
    c: Radius(g1) = 1.65
    c: Radius(g2) = 1.65
    c: Radius(g3) = 1.65
    c: Radius(g4) = 1.65
    c: Radius(g5) = 1.65
    c: Radius(g6) = 1.65
    c: Radius(g7) = 1.65
FEATURE [PartDesign::Pocket] Pocket024
  BaseFeature = -> Chamfer019
  Length = 5
  Length2 = 100
  Profile = -> Sketch033
  Type = 1
FEATURE [Sketcher::SketchObject] Sketch034
  FullyConstrained = false
  MapMode = 5
  Placement = pos=(162.15,0,0) rot=(0.57735,0.57735,0.57735;2.0944rad)
  Support = -> [Pocket024]
  sketch-geometry (2):
    g0: Circle CenterX=5 CenterY=12 CenterZ=0 NormalX=0 NormalY=0 NormalZ=1 AngleXU=0 Radius=1.65
    g1: Circle CenterX=5 CenterY=4 CenterZ=0 NormalX=0 NormalY=0 NormalZ=1 AngleXU=0 Radius=1.65
  constraints (5):
    c: Radius(g0) = 1.65
    c: Radius(g1) = 1.65
    c: Vertical(g0,g1)
    c: DistanceY(g-1,g1) = 4
    c: DistanceX(g-1,g1) = 5
FEATURE [PartDesign::Pocket] Pocket025
  BaseFeature = -> Pocket024
  Length = 5
  Length2 = 100
  Profile = -> Sketch034
  Type = 1
FEATURE [Sketcher::SketchObject] Sketch035
  FullyConstrained = true
  MapMode = 5
  Support = -> [XY_Plane003]
  expr: Constraints[21] = <<args>>.case_heigh_offset + <<args>>.pixel_h / 2 + 0.15 + 11
  expr: Constraints[20] = <<args>>.pixel_h / 2 - 11
  expr: Constraints[19] = <<args>>.case_width_offset + 0.15
  expr: Constraints[18] = <<args>>.case_width_offset * 2 + <<args>>.pixel_w + 0.3
  sketch-geometry (8):
    g0: LineSegment StartX=-7.15 StartY=27 StartZ=0 EndX=-5.15 EndY=27 EndZ=0
    g1: LineSegment StartX=-5.15 StartY=27 StartZ=0 EndX=-5.15 EndY=83.15 EndZ=0
    g2: LineSegment StartX=-5.15 StartY=83.15 StartZ=0 EndX=160.15 EndY=83.15 EndZ=0
    g3: LineSegment StartX=160.15 StartY=83.15 StartZ=0 EndX=160.15 EndY=27 EndZ=0
    g4: LineSegment StartX=160.15 StartY=27 StartZ=0 EndX=162.15 EndY=27 EndZ=0
    g5: LineSegment StartX=162.15 StartY=27 StartZ=0 EndX=162.15 EndY=85.15 EndZ=0
    g6: LineSegment StartX=162.15 StartY=85.15 StartZ=0 EndX=-7.15 EndY=85.15 EndZ=0
    g7: LineSegment StartX=-7.15 StartY=85.15 StartZ=0 EndX=-7.15 EndY=27 EndZ=0
  constraints (24):
    c: Coincident(g0,g1)
    c: Vertical(g1)
    c: Coincident(g1,g2)
    c: Horizontal(g2)
    c: Coincident(g2,g3)
    c: Vertical(g3)
    c: Coincident(g3,g4)
    c: Horizontal(g4)
    c: Coincident(g4,g5)
    c: Vertical(g5)
    c: Coincident(g5,g6)
    c: Horizontal(g6)
    c: Coincident(g6,g7)
    c: Coincident(g7,g0)
    c: Vertical(g7)
    c: Horizontal(g0)
    c: DistanceX(g0,g0) = 2
    c: DistanceX(g4,g4) = 2
    c: DistanceX(g2,g2) = 165.3
    c: DistanceX(g0,g-1) = 5.15
    c: DistanceY(g-1,g0) = 27
    c: DistanceY(g1,g1) = 56.15
    c: DistanceY(g1,g6) = 2
    c: Horizontal(g3,g0)
FEATURE [PartDesign::Pad] Pad008
  Direction = (1,1,1)
  Length = 33
  Length2 = 100
  Profile = -> Sketch035
  Type = 0
  expr: Length = <<args>>.case_thickness + <<args>>.back_thickness + <<args>>.sun_visor_heigh
FEATURE [PartDesign::Chamfer] Chamfer021
  Angle = 45
  Base = -> Pad008 [Edge5,Edge8]
  BaseFeature = -> Pad008
  ChamferType = 0
  FlipDirection = false
  Size = 3
  Size2 = 1
  SupportTransform = false
FEATURE [PartDesign::Fillet] Fillet009
  Base = -> Chamfer021 [Edge2,Edge14,Edge25,Edge27]
  BaseFeature = -> Chamfer021
  Radius = 2
  SupportTransform = false
FEATURE [PartDesign::Chamfer] Chamfer022
  Angle = 45
  Base = -> Fillet009 [Edge34,Edge36]
  BaseFeature = -> Fillet009
  ChamferType = 0
  FlipDirection = false
  Size = 3.5
  Size2 = 1
  SupportTransform = false
FEATURE [Sketcher::SketchObject] Sketch036
  FullyConstrained = true
  MapMode = 5
  Placement = pos=(0,85.15,0) rot=(0,0.707107,0.707107;3.14159rad)
  Support = -> [Chamfer022]
  expr: Constraints[25] = <<args>>.button_volume_width
  expr: Constraints[24] = <<args>>.button_volume_offset
  expr: Constraints[23] = <<args>>.pixel_t - 2 + 0.2
  expr: Constraints[13] = <<args>>.pixel_w
  expr: Constraints[11] = <<args>>.button_power_width
  expr: Constraints[10] = <<args>>.button_power_offset
  expr: Constraints[22] = <<args>>.back_thickness + 1
  expr: Constraints[9] = <<args>>.pixel_t - 2 + 0.2
  expr: Constraints[8] = <<args>>.back_thickness + 1
  sketch-geometry (15):
    g0: LineSegment StartX=-47 StartY=15.2 StartZ=0 EndX=-37 EndY=15.2 EndZ=0
    g1: LineSegment StartX=-37 StartY=15.2 StartZ=0 EndX=-37 EndY=9 EndZ=0
    g2: LineSegment StartX=-37 StartY=9 StartZ=0 EndX=-47 EndY=9 EndZ=0
    g3: LineSegment StartX=-47 StartY=9 StartZ=0 EndX=-47 EndY=15.2 EndZ=0
    g4: GeomPoint X=-155 Y=0 Z=0
    g5: LineSegment StartX=-79 StartY=15.2 StartZ=0 EndX=-59 EndY=15.2 EndZ=0
    g6: LineSegment StartX=-59 StartY=15.2 StartZ=0 EndX=-59 EndY=9 EndZ=0
    g7: LineSegment StartX=-59 StartY=9 StartZ=0 EndX=-79 EndY=9 EndZ=0
    g8: LineSegment StartX=-79 StartY=9 StartZ=0 EndX=-79 EndY=15.2 EndZ=0
    g9: Circle CenterX=-135 CenterY=12 CenterZ=0 NormalX=0 NormalY=0 NormalZ=1 AngleXU=0 Radius=1.65
    g10: Circle CenterX=-135 CenterY=4 CenterZ=0 NormalX=0 NormalY=0 NormalZ=1 AngleXU=0 Radius=1.65
    g11: Circle CenterX=-90 CenterY=12 CenterZ=0 NormalX=0 NormalY=0 NormalZ=1 AngleXU=0 Radius=1.65
    g12: Circle CenterX=-90 CenterY=4 CenterZ=0 NormalX=0 NormalY=0 NormalZ=1 AngleXU=0 Radius=1.65
    g13: Circle CenterX=-20 CenterY=12 CenterZ=0 NormalX=0 NormalY=0 NormalZ=1 AngleXU=0 Radius=1.65
    g14: Circle CenterX=-20 CenterY=4 CenterZ=0 NormalX=0 NormalY=0 NormalZ=1 AngleXU=0 Radius=1.65
  constraints (44):
    c: Coincident(g0,g1)
    c: Coincident(g1,g2)
    c: Coincident(g2,g3)
    c: Coincident(g3,g0)
    c: Horizontal(g0)
    c: Horizontal(g2)
    c: Vertical(g1)
    c: Vertical(g3)
    c: DistanceY(g-1,g1) = 9
    c: DistanceY(g1,g1) = 6.2
    c: DistanceX(g1,g-1) = 37
    c: DistanceX(g2,g2) = 10
    c: PointOnObject(g4,g-1)
    c: DistanceX(g4,g-1) = 155
    c: Coincident(g5,g6)
    c: Coincident(g6,g7)
    c: Coincident(g7,g8)
    c: Coincident(g8,g5)
    c: Horizontal(g5)
    c: Horizontal(g7)
    c: Vertical(g6)
    c: Vertical(g8)
    c: DistanceY(g-1,g6) = 9
    c: DistanceY(g6,g6) = 6.2
    c: DistanceX(g6,g-1) = 59
    c: DistanceX(g5,g5) = 20
    c: Radius(g9) = 1.65
    c: Radius(g10) = 1.65
    c: Radius(g11) = 1.65
    c: Radius(g12) = 1.65
    c: Radius(g13) = 1.65
    c: Radius(g14) = 1.65
    c: Vertical(g9,g10)
    c: Vertical(g11,g12)
    c: Vertical(g13,g14)
    c: Horizontal(g9,g11)
    c: Horizontal(g11,g13)
    c: Horizontal(g10,g12)
    c: Horizontal(g12,g14)
    c: DistanceX(g14,g-1) = 20
    c: DistanceY(g-1,g14) = 4
    c: DistanceY(g14,g13) = 8
    c: DistanceX(g4,g10) = 20
    c: DistanceX(g10,g12) = 45
FEATURE [PartDesign::Pocket] Pocket026
  BaseFeature = -> Chamfer022
  Length = 5
  Length2 = 100
  Profile = -> Sketch036
  Type = 1
FEATURE [Sketcher::SketchObject] Sketch037
  FullyConstrained = true
  MapMode = 5
  Placement = pos=(162.15,0,0) rot=(0.57735,0.57735,0.57735;2.0944rad)
  Support = -> [Pocket026]
  expr: Constraints[11] = <<args>>.pixel_h
  sketch-geometry (7):
    g0: Circle CenterX=44 CenterY=12 CenterZ=0 NormalX=0 NormalY=0 NormalZ=1 AngleXU=0 Radius=1.65
    g1: Circle CenterX=44 CenterY=4 CenterZ=0 NormalX=0 NormalY=0 NormalZ=1 AngleXU=0 Radius=1.65
    g2: Circle CenterX=71 CenterY=12 CenterZ=0 NormalX=0 NormalY=0 NormalZ=1 AngleXU=0 Radius=1.65
    g3: Circle CenterX=71 CenterY=4 CenterZ=0 NormalX=0 NormalY=0 NormalZ=1 AngleXU=0 Radius=1.65
    g4: GeomPoint X=76 Y=0 Z=0
    g5: Circle CenterX=32 CenterY=12 CenterZ=0 NormalX=0 NormalY=0 NormalZ=1 AngleXU=0 Radius=1.65
    g6: Circle CenterX=32 CenterY=4 CenterZ=0 NormalX=0 NormalY=0 NormalZ=1 AngleXU=0 Radius=1.65
  constraints (20):
    c: Radius(g0) = 1.65
    c: Radius(g1) = 1.65
    c: Radius(g3) = 1.65
    c: Radius(g2) = 1.65
    c: Vertical(g0,g1)
    c: Vertical(g2,g3)
    c: Horizontal(g0,g2)
    c: Horizontal(g1,g3)
    c: DistanceY(g1,g0) = 8
    c: DistanceY(g-1,g1) = 4
    c: PointOnObject(g4,g-1)
    c: DistanceX(g-1,g4) = 76
    c: DistanceX(g3,g4) = 5
    c: DistanceX(g1,g3) = 27
    c: Radius(g5) = 1.65
    c: Radius(g6) = 1.65
    c: Vertical(g6,g5)
    c: Horizontal(g5,g0)
    c: DistanceX(g5,g0) = 12
    c: Horizontal(g6,g1)
FEATURE [PartDesign::Pocket] Pocket027
  BaseFeature = -> Pocket026
  Length = 5
  Length2 = 100
  Profile = -> Sketch037
  Type = 1
FEATURE [Sketcher::SketchObject] Sketch038
  FullyConstrained = true
  MapMode = 5
  Placement = pos=(162.15,0,0) rot=(0.57735,0.57735,0.57735;2.0944rad)
  Support = -> [Pocket027]
  expr: Constraints[4] = <<args>>.sun_visor_ramp_width
  expr: Constraints[5] = <<args>>.case_thickness + <<args>>.back_thickness + <<args>>.sun_visor_heigh
  sketch-geometry (3):
    g0: LineSegment StartX=27 StartY=17 StartZ=0 EndX=67 EndY=33 EndZ=0
    g1: LineSegment StartX=27 StartY=33 StartZ=0 EndX=27 EndY=17 EndZ=0
    g2: LineSegment StartX=27 StartY=33 StartZ=0 EndX=67 EndY=33 EndZ=0
  constraints (9):
    c: Coincident(g1,g0)
    c: Vertical(g1)
    c: DistanceX(g-1,g0) = 27
    c: DistanceY(g-1,g0) = 17
    c: DistanceX(g0,g0) = 40
    c: DistanceY(g-1,g1) = 33
    c: Coincident(g2,g1)
    c: Coincident(g2,g0)
    c: Horizontal(g2)
FEATURE [PartDesign::Pocket] Pocket028
  BaseFeature = -> Pocket027
  Length = 5
  Length2 = 100
  Profile = -> Sketch038
  Type = 1
FEATURE [PartDesign::Chamfer] Chamfer023
  Angle = 45
  Base = -> Pocket025 [Edge77,Edge76,Edge101,Edge105,Edge104,Edge100,Edge103,Edge99,Edge98,Edge102,Edge133,Edge134]
  BaseFeature = -> Pocket025
  ChamferType = 0
  FlipDirection = false
  Size = 0.4
  Size2 = 1
  SupportTransform = false
FEATURE [PartDesign::Body] Body004014  label="bottom-cover"
  Group = -> [Sketch032,Pad007,Chamfer016,Fillet,Chamfer017,Fillet008,Chamfer018,Chamfer019,Sketch033,Pocket024,Sketch034,Pocket025,Chamfer023]
  Origin = -> Origin002
  Placement = pos=(0,0,-8) rot=(0,0,1;0rad)
  Tip = -> Chamfer023
  expr: .Placement.Base.z = -<<args>>.back_thickness
FEATURE [Sketcher::SketchObject] Sketch039
  FullyConstrained = true
  MapMode = 5
  Placement = pos=(162.15,0,0) rot=(0.57735,0.57735,0.57735;2.0944rad)
  Support = -> [Pocket028]
  expr: Constraints[8] = <<args>>.speaker_width + 4
  expr: Constraints[9] = <<args>>.pixel_h - <<args>>.spekaer_offset + 2
  expr: Constraints[10] = <<args>>.pixel_t - 2 + 0.2
  expr: Constraints[11] = <<args>>.back_thickness + 1
  sketch-geometry (4):
    g0: LineSegment StartX=49 StartY=15.2 StartZ=0 EndX=64 EndY=15.2 EndZ=0
    g1: LineSegment StartX=64 StartY=15.2 StartZ=0 EndX=64 EndY=9 EndZ=0
    g2: LineSegment StartX=64 StartY=9 StartZ=0 EndX=49 EndY=9 EndZ=0
    g3: LineSegment StartX=49 StartY=9 StartZ=0 EndX=49 EndY=15.2 EndZ=0
  constraints (12):
    c: Coincident(g0,g1)
    c: Coincident(g1,g2)
    c: Coincident(g2,g3)
    c: Coincident(g3,g0)
    c: Horizontal(g0)
    c: Horizontal(g2)
    c: Vertical(g1)
    c: Vertical(g3)
    c: DistanceX(g0,g0) = 15
    c: DistanceX(g-1,g1) = 64
    c: DistanceY(g3,g3) = 6.2
    c: DistanceY(g-1,g2) = 9
FEATURE [PartDesign::Pocket] Pocket029
  BaseFeature = -> Pocket028
  Length = 2
  Length2 = 100
  Profile = -> Sketch039
  Type = 0
FEATURE [PartDesign::Fillet] Fillet010
  Base = -> Pocket029 [Edge30,Edge75,Edge113,Edge114]
  BaseFeature = -> Pocket029
  Radius = 3
  SupportTransform = false
FEATURE [PartDesign::Chamfer] Chamfer024
  Angle = 45
  Base = -> Fillet010 [Edge26,Edge16]
  BaseFeature = -> Fillet010
  ChamferType = 0
  FlipDirection = false
  Size = 1
  Size2 = 1
  SupportTransform = false
FEATURE [PartDesign::Fillet] Fillet011
  Base = -> Chamfer024 [Edge38,Edge6,Edge84,Edge68]
  BaseFeature = -> Chamfer024
  Radius = 2
  SupportTransform = false
FEATURE [PartDesign::Chamfer] Chamfer025
  Angle = 45
  Base = -> Fillet011 [Edge116,Edge120,Edge121,Edge128,Edge127,Edge126,Edge129,Edge125,Edge122,Edge123,Edge124,Edge115,Edge29,Edge27,Edge25,Edge23,Edge21,Edge80,Edge91,Edge81,Edge92,Edge84,Edge85,Edge82,Edge83,Edge89,Edge88,Edge87,Edge86,Edge90,Edge93,Edge9,Edge12,Edge10,Edge13,Edge11,Edge14,Edge118,Edge119,Edge117,+46 more]
  BaseFeature = -> Fillet011
  ChamferType = 0
  FlipDirection = false
  Size = 0.4
  Size2 = 1
  SupportTransform = false
FEATURE [PartDesign::Body] Body004015  label="top-cover"
  Group = -> [Sketch035,Pad008,Chamfer021,Fillet009,Chamfer022,Sketch036,Pocket026,Sketch037,Pocket027,Sketch038,Pocket028,Sketch039,Pocket029,Fillet010,Chamfer024,Fillet011,Chamfer025]
  Origin = -> Origin003
  Placement = pos=(0,0,-8) rot=(0,0,1;0rad)
  Tip = -> Chamfer025
  expr: .Placement.Base.z = -<<args>>.back_thickness
FEATURE [Sketcher::SketchObject] Sketch040
  FullyConstrained = true
  MapMode = 5
  Support = -> [DatumPlane006]
  expr: Constraints[9] = <<args>>.pixel_h - 9
  expr: Constraints[8] = <<args>>.wiring_hole_offset - 20
  sketch-geometry (4):
    g0: ArcOfCircle CenterX=90 CenterY=67 CenterZ=0 NormalX=0 NormalY=0 NormalZ=1 AngleXU=0 Radius=1.5 StartAngle=1.5708 EndAngle=4.71239
    g1: ArcOfCircle CenterX=100 CenterY=67 CenterZ=0 NormalX=0 NormalY=0 NormalZ=1 AngleXU=0 Radius=1.5 StartAngle=4.71239 EndAngle=7.85398
    g2: LineSegment StartX=90 StartY=65.5 StartZ=0 EndX=100 EndY=65.5 EndZ=0
    g3: LineSegment StartX=90 StartY=68.5 StartZ=0 EndX=100 EndY=68.5 EndZ=0
  constraints (10):
    c: Tangent(g0,g3) = 1.5708
    c: Tangent(g0,g2) = -1.5708
    c: Tangent(g2,g1) = -1.5708
    c: Tangent(g3,g1) = 1.5708
    c: Horizontal(g2)
    c: Equal(g0,g1)
    c: DistanceX(g0,g1) = 10
    c: Radius(g0) = 1.5
    c: DistanceX(g-1,g1) = 100
    c: DistanceY(g-1,g1) = 67
FEATURE [PartDesign::Pad] Pad009
  BaseFeature = -> Chamfer010
  Direction = (1,1,1)
  Length = 7
  Length2 = 100
  Profile = -> Sketch040
  Type = 0
  expr: Length = <<args>>.back_thickness - 1
FEATURE [Sketcher::SketchObject] Sketch041
  FullyConstrained = true
  MapMode = 5
  Support = -> [DatumPlane006]
  expr: Constraints[8] = <<args>>.headphone_jack_width
  expr: Constraints[9] = <<args>>.headphone_jack_center_offset - <<args>>.headphone_jack_width / 2
  expr: Constraints[10] = <<args>>.case_width_offset
  expr: Constraints[11] = <<args>>.case_width_offset
  sketch-geometry (4):
    g0: LineSegment StartX=-5 StartY=26 StartZ=0 EndX=0 EndY=26 EndZ=0
    g1: LineSegment StartX=-3e-16 StartY=26 StartZ=0 EndX=-3e-16 EndY=18 EndZ=0
    g2: LineSegment StartX=-3e-16 StartY=18 StartZ=0 EndX=-5 EndY=18 EndZ=0
    g3: LineSegment StartX=-5 StartY=18 StartZ=0 EndX=-5 EndY=26 EndZ=0
  constraints (12):
    c: Coincident(g0,g1)
    c: Coincident(g1,g2)
    c: Coincident(g2,g3)
    c: Coincident(g3,g0)
    c: Horizontal(g0)
    c: Horizontal(g2)
    c: Vertical(g1)
    c: Vertical(g3)
    c: DistanceY(g3,g3) = 8
    c: DistanceY(g-1,g2) = 18
    c: DistanceX(g2,g-1) = 5
    c: DistanceX(g2,g2) = 5
FEATURE [PartDesign::Pocket] Pocket030
  BaseFeature = -> Pad009
  Length = 5
  Length2 = 100
  Profile = -> Sketch041
  Reversed = true
  Type = 1
FEATURE [PartDesign::Chamfer] Chamfer026
  Angle = 45
  Base = -> Pocket030 [Edge14]
  BaseFeature = -> Pocket030
  ChamferType = 0
  FlipDirection = false
  Size = 1
  Size2 = 1
  SupportTransform = false
FEATURE [PartDesign::Body] Body002  label="back"
  Group = -> [DatumPlane006,Sketch011,Pad001,DatumPlane007,Sketch012,Pocket009,DatumPlane009,DatumPlane010,DatumPlane011,DatumPlane012,Sketch013,Pad002,Sketch014,Pad003,Sketch016,Pocket011,Sketch017,Pocket012,Sketch020,Pocket015,Sketch021,Pad004,Sketch023,Pocket017,Sketch024,Pad005,Fillet006,Chamfer006,Fillet007,Chamfer007,Sketch025,Pad006,Chamfer008,Sketch028,Pocket020,Sketch029,Pocket021,Sketch030,Pocket022,+9 more]
  Origin = -> Origin001
  Placement = pos=(0,0,-8) rot=(0,0,1;0rad)
  Tip = -> Chamfer026
  expr: .Placement.Base.z = -<<args>>.back_thickness
FEATURE [PartDesign::Chamfer] Chamfer027
  Angle = 45
  Base = -> Chamfer009 [Edge213,Edge99]
  BaseFeature = -> Chamfer009
  ChamferType = 0
  FlipDirection = false
  Size = 1
  Size2 = 1
  SupportTransform = false
FEATURE [PartDesign::Body] Body  label="front"
  Group = -> [Sketch,Pad,DatumPlane,Sketch001,Pocket,DatumPlane001,Sketch002,Pocket001,Sketch003,Pocket002,Sketch005,Pocket003,DatumPlane002,Sketch007,Pocket005,DatumPlane003,Sketch008,Pocket006,DatumPlane004,Sketch009,Pocket007,DatumPlane005,Sketch010,Pocket008,Sketch015,Pocket010,Fillet004,Chamfer003,Chamfer004,Fillet005,Chamfer005,Sketch026,Pocket018,Sketch027,Pocket019,Chamfer009,Chamfer027]
  Origin = -> Origin
  Tip = -> Chamfer027
FEATURE [Part::Feature] Chamfer027001
  shape: bbox 165 x 90 x 10 mm, 139 faces (baked)
FEATURE [Part::Feature] Pocket008001  label="top-pocket001"
  shape: bbox 165 x 90 x 10 mm, 54 faces (baked)
